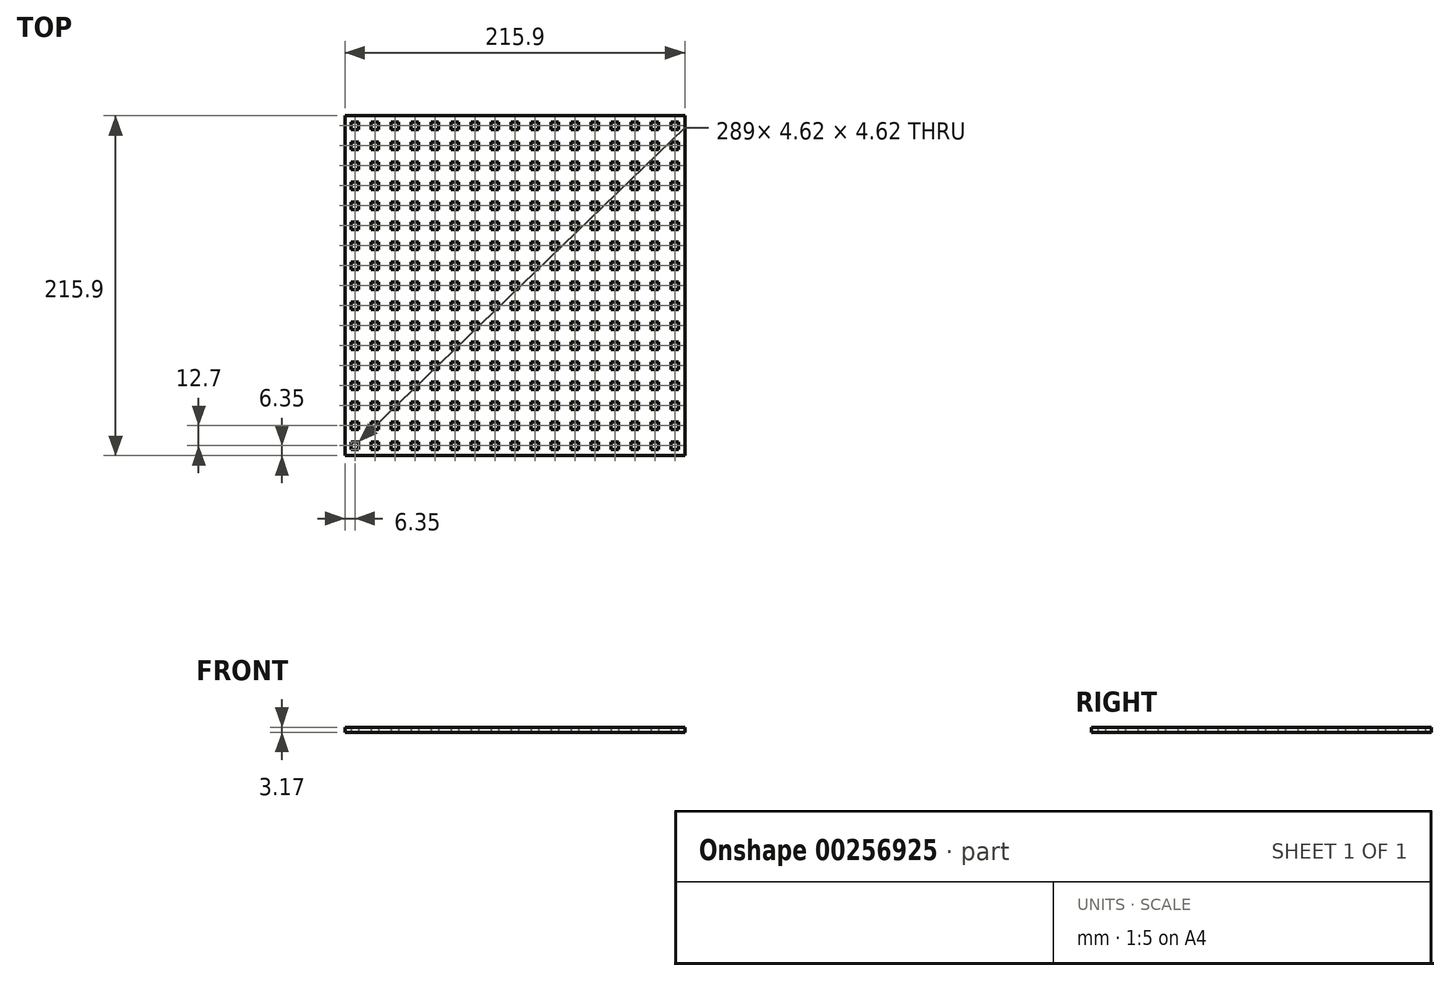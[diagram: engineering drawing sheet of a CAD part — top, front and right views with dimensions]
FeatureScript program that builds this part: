
annotation { "Feature Type Name" : "Feature", "Feature Type Description" : "" }
export const myFeature = defineFeature(function(context is Context, id is Id, definition is map)
    precondition{}
    {
        {
            var Q0;
            Q0=qCreatedBy(makeId("Top.planeOp"),FACE);
            var sketch = newSketch(context, id + "F0", { "sketchPlane" : qUnion([Q0])});
            skLineSegment(sketch, "E0.bottom", {"start": v(107.95, 107.95) * mm, "end": v(-107.95, 107.95) * mm});
            skLineSegment(sketch, "E0.top", {"start": v(107.95, -107.95) * mm, "end": v(-107.95, -107.95) * mm});
            skLineSegment(sketch, "E0.left", {"start": v(107.95, 107.95) * mm, "end": v(107.95, -107.95) * mm});
            skLineSegment(sketch, "E0.right", {"start": v(-107.95, 107.95) * mm, "end": v(-107.95, -107.95) * mm});
            skPoint(sketch, "E0.middle", {"position": v(0, 0) * mm});
            skLineSegment(sketch, "E1.bottom", {"start": v(-107.95, -107.95) * mm, "end": v(-101.6, -107.95) * mm});
            skLineSegment(sketch, "E1.left", {"start": v(-107.95, -107.95) * mm, "end": v(-107.95, -101.6) * mm});
            skLineSegment(sketch, "E2.bottom", {"start": v(-99.29, -103.91) * mm, "end": v(-103.91, -103.91) * mm});
            skLineSegment(sketch, "E2.top", {"start": v(-99.29, -99.29) * mm, "end": v(-103.91, -99.29) * mm});
            skLineSegment(sketch, "E2.left", {"start": v(-99.29, -103.91) * mm, "end": v(-99.29, -99.29) * mm});
            skLineSegment(sketch, "E2.right", {"start": v(-103.91, -103.91) * mm, "end": v(-103.91, -99.29) * mm});
            skPoint(sketch, "E2.middle", {"position": v(-101.6, -101.6) * mm});
            skLineSegment(sketch, "E3.0.1.0", {"start": v(-99.29, -86.59) * mm, "end": v(-103.91, -86.59) * mm});
            skLineSegment(sketch, "E3.0.1.1", {"start": v(-99.29, -91.21) * mm, "end": v(-99.29, -86.59) * mm});
            skLineSegment(sketch, "E3.0.1.2", {"start": v(-99.29, -91.21) * mm, "end": v(-103.91, -91.21) * mm});
            skLineSegment(sketch, "E3.0.1.3", {"start": v(-103.91, -91.21) * mm, "end": v(-103.91, -86.59) * mm});
            skLineSegment(sketch, "E3.0.2.0", {"start": v(-99.29, -73.89) * mm, "end": v(-103.91, -73.89) * mm});
            skLineSegment(sketch, "E3.0.2.1", {"start": v(-99.29, -78.51) * mm, "end": v(-99.29, -73.89) * mm});
            skLineSegment(sketch, "E3.0.2.2", {"start": v(-99.29, -78.51) * mm, "end": v(-103.91, -78.51) * mm});
            skLineSegment(sketch, "E3.0.2.3", {"start": v(-103.91, -78.51) * mm, "end": v(-103.91, -73.89) * mm});
            skLineSegment(sketch, "E3.0.3.0", {"start": v(-99.29, -61.19) * mm, "end": v(-103.91, -61.19) * mm});
            skLineSegment(sketch, "E3.0.3.1", {"start": v(-99.29, -65.81) * mm, "end": v(-99.29, -61.19) * mm});
            skLineSegment(sketch, "E3.0.3.2", {"start": v(-99.29, -65.81) * mm, "end": v(-103.91, -65.81) * mm});
            skLineSegment(sketch, "E3.0.3.3", {"start": v(-103.91, -65.81) * mm, "end": v(-103.91, -61.19) * mm});
            skLineSegment(sketch, "E3.0.4.0", {"start": v(-99.29, -48.49) * mm, "end": v(-103.91, -48.49) * mm});
            skLineSegment(sketch, "E3.0.4.1", {"start": v(-99.29, -53.11) * mm, "end": v(-99.29, -48.49) * mm});
            skLineSegment(sketch, "E3.0.4.2", {"start": v(-99.29, -53.11) * mm, "end": v(-103.91, -53.11) * mm});
            skLineSegment(sketch, "E3.0.4.3", {"start": v(-103.91, -53.11) * mm, "end": v(-103.91, -48.49) * mm});
            skLineSegment(sketch, "E3.0.5.0", {"start": v(-99.29, -35.79) * mm, "end": v(-103.91, -35.79) * mm});
            skLineSegment(sketch, "E3.0.5.1", {"start": v(-99.29, -40.41) * mm, "end": v(-99.29, -35.79) * mm});
            skLineSegment(sketch, "E3.0.5.2", {"start": v(-99.29, -40.41) * mm, "end": v(-103.91, -40.41) * mm});
            skLineSegment(sketch, "E3.0.5.3", {"start": v(-103.91, -40.41) * mm, "end": v(-103.91, -35.79) * mm});
            skLineSegment(sketch, "E3.0.6.0", {"start": v(-99.29, -23.09) * mm, "end": v(-103.91, -23.09) * mm});
            skLineSegment(sketch, "E3.0.6.1", {"start": v(-99.29, -27.71) * mm, "end": v(-99.29, -23.09) * mm});
            skLineSegment(sketch, "E3.0.6.2", {"start": v(-99.29, -27.71) * mm, "end": v(-103.91, -27.71) * mm});
            skLineSegment(sketch, "E3.0.6.3", {"start": v(-103.91, -27.71) * mm, "end": v(-103.91, -23.09) * mm});
            skLineSegment(sketch, "E3.0.7.0", {"start": v(-99.29, -10.39) * mm, "end": v(-103.91, -10.39) * mm});
            skLineSegment(sketch, "E3.0.7.1", {"start": v(-99.29, -15.01) * mm, "end": v(-99.29, -10.39) * mm});
            skLineSegment(sketch, "E3.0.7.2", {"start": v(-99.29, -15.01) * mm, "end": v(-103.91, -15.01) * mm});
            skLineSegment(sketch, "E3.0.7.3", {"start": v(-103.91, -15.01) * mm, "end": v(-103.91, -10.39) * mm});
            skLineSegment(sketch, "E3.0.8.0", {"start": v(-99.29, 2.31) * mm, "end": v(-103.91, 2.31) * mm});
            skLineSegment(sketch, "E3.0.8.1", {"start": v(-99.29, -2.31) * mm, "end": v(-99.29, 2.31) * mm});
            skLineSegment(sketch, "E3.0.8.2", {"start": v(-99.29, -2.31) * mm, "end": v(-103.91, -2.31) * mm});
            skLineSegment(sketch, "E3.0.8.3", {"start": v(-103.91, -2.31) * mm, "end": v(-103.91, 2.31) * mm});
            skLineSegment(sketch, "E3.0.9.0", {"start": v(-99.29, 15.01) * mm, "end": v(-103.91, 15.01) * mm});
            skLineSegment(sketch, "E3.0.9.1", {"start": v(-99.29, 10.39) * mm, "end": v(-99.29, 15.01) * mm});
            skLineSegment(sketch, "E3.0.9.2", {"start": v(-99.29, 10.39) * mm, "end": v(-103.91, 10.39) * mm});
            skLineSegment(sketch, "E3.0.9.3", {"start": v(-103.91, 10.39) * mm, "end": v(-103.91, 15.01) * mm});
            skLineSegment(sketch, "E3.0.10.0", {"start": v(-99.29, 27.71) * mm, "end": v(-103.91, 27.71) * mm});
            skLineSegment(sketch, "E3.0.10.1", {"start": v(-99.29, 23.09) * mm, "end": v(-99.29, 27.71) * mm});
            skLineSegment(sketch, "E3.0.10.2", {"start": v(-99.29, 23.09) * mm, "end": v(-103.91, 23.09) * mm});
            skLineSegment(sketch, "E3.0.10.3", {"start": v(-103.91, 23.09) * mm, "end": v(-103.91, 27.71) * mm});
            skLineSegment(sketch, "E3.0.11.0", {"start": v(-99.29, 40.41) * mm, "end": v(-103.91, 40.41) * mm});
            skLineSegment(sketch, "E3.0.11.1", {"start": v(-99.29, 35.79) * mm, "end": v(-99.29, 40.41) * mm});
            skLineSegment(sketch, "E3.0.11.2", {"start": v(-99.29, 35.79) * mm, "end": v(-103.91, 35.79) * mm});
            skLineSegment(sketch, "E3.0.11.3", {"start": v(-103.91, 35.79) * mm, "end": v(-103.91, 40.41) * mm});
            skLineSegment(sketch, "E3.0.12.0", {"start": v(-99.29, 53.11) * mm, "end": v(-103.91, 53.11) * mm});
            skLineSegment(sketch, "E3.0.12.1", {"start": v(-99.29, 48.49) * mm, "end": v(-99.29, 53.11) * mm});
            skLineSegment(sketch, "E3.0.12.2", {"start": v(-99.29, 48.49) * mm, "end": v(-103.91, 48.49) * mm});
            skLineSegment(sketch, "E3.0.12.3", {"start": v(-103.91, 48.49) * mm, "end": v(-103.91, 53.11) * mm});
            skLineSegment(sketch, "E3.0.13.0", {"start": v(-99.29, 65.81) * mm, "end": v(-103.91, 65.81) * mm});
            skLineSegment(sketch, "E3.0.13.1", {"start": v(-99.29, 61.19) * mm, "end": v(-99.29, 65.81) * mm});
            skLineSegment(sketch, "E3.0.13.2", {"start": v(-99.29, 61.19) * mm, "end": v(-103.91, 61.19) * mm});
            skLineSegment(sketch, "E3.0.13.3", {"start": v(-103.91, 61.19) * mm, "end": v(-103.91, 65.81) * mm});
            skLineSegment(sketch, "E3.0.14.0", {"start": v(-99.29, 78.51) * mm, "end": v(-103.91, 78.51) * mm});
            skLineSegment(sketch, "E3.0.14.1", {"start": v(-99.29, 73.89) * mm, "end": v(-99.29, 78.51) * mm});
            skLineSegment(sketch, "E3.0.14.2", {"start": v(-99.29, 73.89) * mm, "end": v(-103.91, 73.89) * mm});
            skLineSegment(sketch, "E3.0.14.3", {"start": v(-103.91, 73.89) * mm, "end": v(-103.91, 78.51) * mm});
            skLineSegment(sketch, "E3.0.15.0", {"start": v(-99.29, 91.21) * mm, "end": v(-103.91, 91.21) * mm});
            skLineSegment(sketch, "E3.0.15.1", {"start": v(-99.29, 86.59) * mm, "end": v(-99.29, 91.21) * mm});
            skLineSegment(sketch, "E3.0.15.2", {"start": v(-99.29, 86.59) * mm, "end": v(-103.91, 86.59) * mm});
            skLineSegment(sketch, "E3.0.15.3", {"start": v(-103.91, 86.59) * mm, "end": v(-103.91, 91.21) * mm});
            skLineSegment(sketch, "E3.0.16.0", {"start": v(-99.29, 103.91) * mm, "end": v(-103.91, 103.91) * mm});
            skLineSegment(sketch, "E3.0.16.1", {"start": v(-99.29, 99.29) * mm, "end": v(-99.29, 103.91) * mm});
            skLineSegment(sketch, "E3.0.16.2", {"start": v(-99.29, 99.29) * mm, "end": v(-103.91, 99.29) * mm});
            skLineSegment(sketch, "E3.0.16.3", {"start": v(-103.91, 99.29) * mm, "end": v(-103.91, 103.91) * mm});
            skLineSegment(sketch, "E3.1.0.0", {"start": v(-86.59, -99.29) * mm, "end": v(-91.21, -99.29) * mm});
            skLineSegment(sketch, "E3.1.0.1", {"start": v(-86.59, -103.91) * mm, "end": v(-86.59, -99.29) * mm});
            skLineSegment(sketch, "E3.1.0.2", {"start": v(-86.59, -103.91) * mm, "end": v(-91.21, -103.91) * mm});
            skLineSegment(sketch, "E3.1.0.3", {"start": v(-91.21, -103.91) * mm, "end": v(-91.21, -99.29) * mm});
            skLineSegment(sketch, "E3.1.1.0", {"start": v(-86.59, -86.59) * mm, "end": v(-91.21, -86.59) * mm});
            skLineSegment(sketch, "E3.1.1.1", {"start": v(-86.59, -91.21) * mm, "end": v(-86.59, -86.59) * mm});
            skLineSegment(sketch, "E3.1.1.2", {"start": v(-86.59, -91.21) * mm, "end": v(-91.21, -91.21) * mm});
            skLineSegment(sketch, "E3.1.1.3", {"start": v(-91.21, -91.21) * mm, "end": v(-91.21, -86.59) * mm});
            skLineSegment(sketch, "E3.1.2.0", {"start": v(-86.59, -73.89) * mm, "end": v(-91.21, -73.89) * mm});
            skLineSegment(sketch, "E3.1.2.1", {"start": v(-86.59, -78.51) * mm, "end": v(-86.59, -73.89) * mm});
            skLineSegment(sketch, "E3.1.2.2", {"start": v(-86.59, -78.51) * mm, "end": v(-91.21, -78.51) * mm});
            skLineSegment(sketch, "E3.1.2.3", {"start": v(-91.21, -78.51) * mm, "end": v(-91.21, -73.89) * mm});
            skLineSegment(sketch, "E3.1.3.0", {"start": v(-86.59, -61.19) * mm, "end": v(-91.21, -61.19) * mm});
            skLineSegment(sketch, "E3.1.3.1", {"start": v(-86.59, -65.81) * mm, "end": v(-86.59, -61.19) * mm});
            skLineSegment(sketch, "E3.1.3.2", {"start": v(-86.59, -65.81) * mm, "end": v(-91.21, -65.81) * mm});
            skLineSegment(sketch, "E3.1.3.3", {"start": v(-91.21, -65.81) * mm, "end": v(-91.21, -61.19) * mm});
            skLineSegment(sketch, "E3.1.4.0", {"start": v(-86.59, -48.49) * mm, "end": v(-91.21, -48.49) * mm});
            skLineSegment(sketch, "E3.1.4.1", {"start": v(-86.59, -53.11) * mm, "end": v(-86.59, -48.49) * mm});
            skLineSegment(sketch, "E3.1.4.2", {"start": v(-86.59, -53.11) * mm, "end": v(-91.21, -53.11) * mm});
            skLineSegment(sketch, "E3.1.4.3", {"start": v(-91.21, -53.11) * mm, "end": v(-91.21, -48.49) * mm});
            skLineSegment(sketch, "E3.1.5.0", {"start": v(-86.59, -35.79) * mm, "end": v(-91.21, -35.79) * mm});
            skLineSegment(sketch, "E3.1.5.1", {"start": v(-86.59, -40.41) * mm, "end": v(-86.59, -35.79) * mm});
            skLineSegment(sketch, "E3.1.5.2", {"start": v(-86.59, -40.41) * mm, "end": v(-91.21, -40.41) * mm});
            skLineSegment(sketch, "E3.1.5.3", {"start": v(-91.21, -40.41) * mm, "end": v(-91.21, -35.79) * mm});
            skLineSegment(sketch, "E3.1.6.0", {"start": v(-86.59, -23.09) * mm, "end": v(-91.21, -23.09) * mm});
            skLineSegment(sketch, "E3.1.6.1", {"start": v(-86.59, -27.71) * mm, "end": v(-86.59, -23.09) * mm});
            skLineSegment(sketch, "E3.1.6.2", {"start": v(-86.59, -27.71) * mm, "end": v(-91.21, -27.71) * mm});
            skLineSegment(sketch, "E3.1.6.3", {"start": v(-91.21, -27.71) * mm, "end": v(-91.21, -23.09) * mm});
            skLineSegment(sketch, "E3.1.7.0", {"start": v(-86.59, -10.39) * mm, "end": v(-91.21, -10.39) * mm});
            skLineSegment(sketch, "E3.1.7.1", {"start": v(-86.59, -15.01) * mm, "end": v(-86.59, -10.39) * mm});
            skLineSegment(sketch, "E3.1.7.2", {"start": v(-86.59, -15.01) * mm, "end": v(-91.21, -15.01) * mm});
            skLineSegment(sketch, "E3.1.7.3", {"start": v(-91.21, -15.01) * mm, "end": v(-91.21, -10.39) * mm});
            skLineSegment(sketch, "E3.1.8.0", {"start": v(-86.59, 2.31) * mm, "end": v(-91.21, 2.31) * mm});
            skLineSegment(sketch, "E3.1.8.1", {"start": v(-86.59, -2.31) * mm, "end": v(-86.59, 2.31) * mm});
            skLineSegment(sketch, "E3.1.8.2", {"start": v(-86.59, -2.31) * mm, "end": v(-91.21, -2.31) * mm});
            skLineSegment(sketch, "E3.1.8.3", {"start": v(-91.21, -2.31) * mm, "end": v(-91.21, 2.31) * mm});
            skLineSegment(sketch, "E3.1.9.0", {"start": v(-86.59, 15.01) * mm, "end": v(-91.21, 15.01) * mm});
            skLineSegment(sketch, "E3.1.9.1", {"start": v(-86.59, 10.39) * mm, "end": v(-86.59, 15.01) * mm});
            skLineSegment(sketch, "E3.1.9.2", {"start": v(-86.59, 10.39) * mm, "end": v(-91.21, 10.39) * mm});
            skLineSegment(sketch, "E3.1.9.3", {"start": v(-91.21, 10.39) * mm, "end": v(-91.21, 15.01) * mm});
            skLineSegment(sketch, "E3.1.10.0", {"start": v(-86.59, 27.71) * mm, "end": v(-91.21, 27.71) * mm});
            skLineSegment(sketch, "E3.1.10.1", {"start": v(-86.59, 23.09) * mm, "end": v(-86.59, 27.71) * mm});
            skLineSegment(sketch, "E3.1.10.2", {"start": v(-86.59, 23.09) * mm, "end": v(-91.21, 23.09) * mm});
            skLineSegment(sketch, "E3.1.10.3", {"start": v(-91.21, 23.09) * mm, "end": v(-91.21, 27.71) * mm});
            skLineSegment(sketch, "E3.1.11.0", {"start": v(-86.59, 40.41) * mm, "end": v(-91.21, 40.41) * mm});
            skLineSegment(sketch, "E3.1.11.1", {"start": v(-86.59, 35.79) * mm, "end": v(-86.59, 40.41) * mm});
            skLineSegment(sketch, "E3.1.11.2", {"start": v(-86.59, 35.79) * mm, "end": v(-91.21, 35.79) * mm});
            skLineSegment(sketch, "E3.1.11.3", {"start": v(-91.21, 35.79) * mm, "end": v(-91.21, 40.41) * mm});
            skLineSegment(sketch, "E3.1.12.0", {"start": v(-86.59, 53.11) * mm, "end": v(-91.21, 53.11) * mm});
            skLineSegment(sketch, "E3.1.12.1", {"start": v(-86.59, 48.49) * mm, "end": v(-86.59, 53.11) * mm});
            skLineSegment(sketch, "E3.1.12.2", {"start": v(-86.59, 48.49) * mm, "end": v(-91.21, 48.49) * mm});
            skLineSegment(sketch, "E3.1.12.3", {"start": v(-91.21, 48.49) * mm, "end": v(-91.21, 53.11) * mm});
            skLineSegment(sketch, "E3.1.13.0", {"start": v(-86.59, 65.81) * mm, "end": v(-91.21, 65.81) * mm});
            skLineSegment(sketch, "E3.1.13.1", {"start": v(-86.59, 61.19) * mm, "end": v(-86.59, 65.81) * mm});
            skLineSegment(sketch, "E3.1.13.2", {"start": v(-86.59, 61.19) * mm, "end": v(-91.21, 61.19) * mm});
            skLineSegment(sketch, "E3.1.13.3", {"start": v(-91.21, 61.19) * mm, "end": v(-91.21, 65.81) * mm});
            skLineSegment(sketch, "E3.1.14.0", {"start": v(-86.59, 78.51) * mm, "end": v(-91.21, 78.51) * mm});
            skLineSegment(sketch, "E3.1.14.1", {"start": v(-86.59, 73.89) * mm, "end": v(-86.59, 78.51) * mm});
            skLineSegment(sketch, "E3.1.14.2", {"start": v(-86.59, 73.89) * mm, "end": v(-91.21, 73.89) * mm});
            skLineSegment(sketch, "E3.1.14.3", {"start": v(-91.21, 73.89) * mm, "end": v(-91.21, 78.51) * mm});
            skLineSegment(sketch, "E3.1.15.0", {"start": v(-86.59, 91.21) * mm, "end": v(-91.21, 91.21) * mm});
            skLineSegment(sketch, "E3.1.15.1", {"start": v(-86.59, 86.59) * mm, "end": v(-86.59, 91.21) * mm});
            skLineSegment(sketch, "E3.1.15.2", {"start": v(-86.59, 86.59) * mm, "end": v(-91.21, 86.59) * mm});
            skLineSegment(sketch, "E3.1.15.3", {"start": v(-91.21, 86.59) * mm, "end": v(-91.21, 91.21) * mm});
            skLineSegment(sketch, "E3.1.16.0", {"start": v(-86.59, 103.91) * mm, "end": v(-91.21, 103.91) * mm});
            skLineSegment(sketch, "E3.1.16.1", {"start": v(-86.59, 99.29) * mm, "end": v(-86.59, 103.91) * mm});
            skLineSegment(sketch, "E3.1.16.2", {"start": v(-86.59, 99.29) * mm, "end": v(-91.21, 99.29) * mm});
            skLineSegment(sketch, "E3.1.16.3", {"start": v(-91.21, 99.29) * mm, "end": v(-91.21, 103.91) * mm});
            skLineSegment(sketch, "E3.2.0.0", {"start": v(-73.89, -99.29) * mm, "end": v(-78.51, -99.29) * mm});
            skLineSegment(sketch, "E3.2.0.1", {"start": v(-73.89, -103.91) * mm, "end": v(-73.89, -99.29) * mm});
            skLineSegment(sketch, "E3.2.0.2", {"start": v(-73.89, -103.91) * mm, "end": v(-78.51, -103.91) * mm});
            skLineSegment(sketch, "E3.2.0.3", {"start": v(-78.51, -103.91) * mm, "end": v(-78.51, -99.29) * mm});
            skLineSegment(sketch, "E3.2.1.0", {"start": v(-73.89, -86.59) * mm, "end": v(-78.51, -86.59) * mm});
            skLineSegment(sketch, "E3.2.1.1", {"start": v(-73.89, -91.21) * mm, "end": v(-73.89, -86.59) * mm});
            skLineSegment(sketch, "E3.2.1.2", {"start": v(-73.89, -91.21) * mm, "end": v(-78.51, -91.21) * mm});
            skLineSegment(sketch, "E3.2.1.3", {"start": v(-78.51, -91.21) * mm, "end": v(-78.51, -86.59) * mm});
            skLineSegment(sketch, "E3.2.2.0", {"start": v(-73.89, -73.89) * mm, "end": v(-78.51, -73.89) * mm});
            skLineSegment(sketch, "E3.2.2.1", {"start": v(-73.89, -78.51) * mm, "end": v(-73.89, -73.89) * mm});
            skLineSegment(sketch, "E3.2.2.2", {"start": v(-73.89, -78.51) * mm, "end": v(-78.51, -78.51) * mm});
            skLineSegment(sketch, "E3.2.2.3", {"start": v(-78.51, -78.51) * mm, "end": v(-78.51, -73.89) * mm});
            skLineSegment(sketch, "E3.2.3.0", {"start": v(-73.89, -61.19) * mm, "end": v(-78.51, -61.19) * mm});
            skLineSegment(sketch, "E3.2.3.1", {"start": v(-73.89, -65.81) * mm, "end": v(-73.89, -61.19) * mm});
            skLineSegment(sketch, "E3.2.3.2", {"start": v(-73.89, -65.81) * mm, "end": v(-78.51, -65.81) * mm});
            skLineSegment(sketch, "E3.2.3.3", {"start": v(-78.51, -65.81) * mm, "end": v(-78.51, -61.19) * mm});
            skLineSegment(sketch, "E3.2.4.0", {"start": v(-73.89, -48.49) * mm, "end": v(-78.51, -48.49) * mm});
            skLineSegment(sketch, "E3.2.4.1", {"start": v(-73.89, -53.11) * mm, "end": v(-73.89, -48.49) * mm});
            skLineSegment(sketch, "E3.2.4.2", {"start": v(-73.89, -53.11) * mm, "end": v(-78.51, -53.11) * mm});
            skLineSegment(sketch, "E3.2.4.3", {"start": v(-78.51, -53.11) * mm, "end": v(-78.51, -48.49) * mm});
            skLineSegment(sketch, "E3.2.5.0", {"start": v(-73.89, -35.79) * mm, "end": v(-78.51, -35.79) * mm});
            skLineSegment(sketch, "E3.2.5.1", {"start": v(-73.89, -40.41) * mm, "end": v(-73.89, -35.79) * mm});
            skLineSegment(sketch, "E3.2.5.2", {"start": v(-73.89, -40.41) * mm, "end": v(-78.51, -40.41) * mm});
            skLineSegment(sketch, "E3.2.5.3", {"start": v(-78.51, -40.41) * mm, "end": v(-78.51, -35.79) * mm});
            skLineSegment(sketch, "E3.2.6.0", {"start": v(-73.89, -23.09) * mm, "end": v(-78.51, -23.09) * mm});
            skLineSegment(sketch, "E3.2.6.1", {"start": v(-73.89, -27.71) * mm, "end": v(-73.89, -23.09) * mm});
            skLineSegment(sketch, "E3.2.6.2", {"start": v(-73.89, -27.71) * mm, "end": v(-78.51, -27.71) * mm});
            skLineSegment(sketch, "E3.2.6.3", {"start": v(-78.51, -27.71) * mm, "end": v(-78.51, -23.09) * mm});
            skLineSegment(sketch, "E3.2.7.0", {"start": v(-73.89, -10.39) * mm, "end": v(-78.51, -10.39) * mm});
            skLineSegment(sketch, "E3.2.7.1", {"start": v(-73.89, -15.01) * mm, "end": v(-73.89, -10.39) * mm});
            skLineSegment(sketch, "E3.2.7.2", {"start": v(-73.89, -15.01) * mm, "end": v(-78.51, -15.01) * mm});
            skLineSegment(sketch, "E3.2.7.3", {"start": v(-78.51, -15.01) * mm, "end": v(-78.51, -10.39) * mm});
            skLineSegment(sketch, "E3.2.8.0", {"start": v(-73.89, 2.31) * mm, "end": v(-78.51, 2.31) * mm});
            skLineSegment(sketch, "E3.2.8.1", {"start": v(-73.89, -2.31) * mm, "end": v(-73.89, 2.31) * mm});
            skLineSegment(sketch, "E3.2.8.2", {"start": v(-73.89, -2.31) * mm, "end": v(-78.51, -2.31) * mm});
            skLineSegment(sketch, "E3.2.8.3", {"start": v(-78.51, -2.31) * mm, "end": v(-78.51, 2.31) * mm});
            skLineSegment(sketch, "E3.2.9.0", {"start": v(-73.89, 15.01) * mm, "end": v(-78.51, 15.01) * mm});
            skLineSegment(sketch, "E3.2.9.1", {"start": v(-73.89, 10.39) * mm, "end": v(-73.89, 15.01) * mm});
            skLineSegment(sketch, "E3.2.9.2", {"start": v(-73.89, 10.39) * mm, "end": v(-78.51, 10.39) * mm});
            skLineSegment(sketch, "E3.2.9.3", {"start": v(-78.51, 10.39) * mm, "end": v(-78.51, 15.01) * mm});
            skLineSegment(sketch, "E3.2.10.0", {"start": v(-73.89, 27.71) * mm, "end": v(-78.51, 27.71) * mm});
            skLineSegment(sketch, "E3.2.10.1", {"start": v(-73.89, 23.09) * mm, "end": v(-73.89, 27.71) * mm});
            skLineSegment(sketch, "E3.2.10.2", {"start": v(-73.89, 23.09) * mm, "end": v(-78.51, 23.09) * mm});
            skLineSegment(sketch, "E3.2.10.3", {"start": v(-78.51, 23.09) * mm, "end": v(-78.51, 27.71) * mm});
            skLineSegment(sketch, "E3.2.11.0", {"start": v(-73.89, 40.41) * mm, "end": v(-78.51, 40.41) * mm});
            skLineSegment(sketch, "E3.2.11.1", {"start": v(-73.89, 35.79) * mm, "end": v(-73.89, 40.41) * mm});
            skLineSegment(sketch, "E3.2.11.2", {"start": v(-73.89, 35.79) * mm, "end": v(-78.51, 35.79) * mm});
            skLineSegment(sketch, "E3.2.11.3", {"start": v(-78.51, 35.79) * mm, "end": v(-78.51, 40.41) * mm});
            skLineSegment(sketch, "E3.2.12.0", {"start": v(-73.89, 53.11) * mm, "end": v(-78.51, 53.11) * mm});
            skLineSegment(sketch, "E3.2.12.1", {"start": v(-73.89, 48.49) * mm, "end": v(-73.89, 53.11) * mm});
            skLineSegment(sketch, "E3.2.12.2", {"start": v(-73.89, 48.49) * mm, "end": v(-78.51, 48.49) * mm});
            skLineSegment(sketch, "E3.2.12.3", {"start": v(-78.51, 48.49) * mm, "end": v(-78.51, 53.11) * mm});
            skLineSegment(sketch, "E3.2.13.0", {"start": v(-73.89, 65.81) * mm, "end": v(-78.51, 65.81) * mm});
            skLineSegment(sketch, "E3.2.13.1", {"start": v(-73.89, 61.19) * mm, "end": v(-73.89, 65.81) * mm});
            skLineSegment(sketch, "E3.2.13.2", {"start": v(-73.89, 61.19) * mm, "end": v(-78.51, 61.19) * mm});
            skLineSegment(sketch, "E3.2.13.3", {"start": v(-78.51, 61.19) * mm, "end": v(-78.51, 65.81) * mm});
            skLineSegment(sketch, "E3.2.14.0", {"start": v(-73.89, 78.51) * mm, "end": v(-78.51, 78.51) * mm});
            skLineSegment(sketch, "E3.2.14.1", {"start": v(-73.89, 73.89) * mm, "end": v(-73.89, 78.51) * mm});
            skLineSegment(sketch, "E3.2.14.2", {"start": v(-73.89, 73.89) * mm, "end": v(-78.51, 73.89) * mm});
            skLineSegment(sketch, "E3.2.14.3", {"start": v(-78.51, 73.89) * mm, "end": v(-78.51, 78.51) * mm});
            skLineSegment(sketch, "E3.2.15.0", {"start": v(-73.89, 91.21) * mm, "end": v(-78.51, 91.21) * mm});
            skLineSegment(sketch, "E3.2.15.1", {"start": v(-73.89, 86.59) * mm, "end": v(-73.89, 91.21) * mm});
            skLineSegment(sketch, "E3.2.15.2", {"start": v(-73.89, 86.59) * mm, "end": v(-78.51, 86.59) * mm});
            skLineSegment(sketch, "E3.2.15.3", {"start": v(-78.51, 86.59) * mm, "end": v(-78.51, 91.21) * mm});
            skLineSegment(sketch, "E3.2.16.0", {"start": v(-73.89, 103.91) * mm, "end": v(-78.51, 103.91) * mm});
            skLineSegment(sketch, "E3.2.16.1", {"start": v(-73.89, 99.29) * mm, "end": v(-73.89, 103.91) * mm});
            skLineSegment(sketch, "E3.2.16.2", {"start": v(-73.89, 99.29) * mm, "end": v(-78.51, 99.29) * mm});
            skLineSegment(sketch, "E3.2.16.3", {"start": v(-78.51, 99.29) * mm, "end": v(-78.51, 103.91) * mm});
            skLineSegment(sketch, "E3.3.0.0", {"start": v(-61.19, -99.29) * mm, "end": v(-65.81, -99.29) * mm});
            skLineSegment(sketch, "E3.3.0.1", {"start": v(-61.19, -103.91) * mm, "end": v(-61.19, -99.29) * mm});
            skLineSegment(sketch, "E3.3.0.2", {"start": v(-61.19, -103.91) * mm, "end": v(-65.81, -103.91) * mm});
            skLineSegment(sketch, "E3.3.0.3", {"start": v(-65.81, -103.91) * mm, "end": v(-65.81, -99.29) * mm});
            skLineSegment(sketch, "E3.3.1.0", {"start": v(-61.19, -86.59) * mm, "end": v(-65.81, -86.59) * mm});
            skLineSegment(sketch, "E3.3.1.1", {"start": v(-61.19, -91.21) * mm, "end": v(-61.19, -86.59) * mm});
            skLineSegment(sketch, "E3.3.1.2", {"start": v(-61.19, -91.21) * mm, "end": v(-65.81, -91.21) * mm});
            skLineSegment(sketch, "E3.3.1.3", {"start": v(-65.81, -91.21) * mm, "end": v(-65.81, -86.59) * mm});
            skLineSegment(sketch, "E3.3.2.0", {"start": v(-61.19, -73.89) * mm, "end": v(-65.81, -73.89) * mm});
            skLineSegment(sketch, "E3.3.2.1", {"start": v(-61.19, -78.51) * mm, "end": v(-61.19, -73.89) * mm});
            skLineSegment(sketch, "E3.3.2.2", {"start": v(-61.19, -78.51) * mm, "end": v(-65.81, -78.51) * mm});
            skLineSegment(sketch, "E3.3.2.3", {"start": v(-65.81, -78.51) * mm, "end": v(-65.81, -73.89) * mm});
            skLineSegment(sketch, "E3.3.3.0", {"start": v(-61.19, -61.19) * mm, "end": v(-65.81, -61.19) * mm});
            skLineSegment(sketch, "E3.3.3.1", {"start": v(-61.19, -65.81) * mm, "end": v(-61.19, -61.19) * mm});
            skLineSegment(sketch, "E3.3.3.2", {"start": v(-61.19, -65.81) * mm, "end": v(-65.81, -65.81) * mm});
            skLineSegment(sketch, "E3.3.3.3", {"start": v(-65.81, -65.81) * mm, "end": v(-65.81, -61.19) * mm});
            skLineSegment(sketch, "E3.3.4.0", {"start": v(-61.19, -48.49) * mm, "end": v(-65.81, -48.49) * mm});
            skLineSegment(sketch, "E3.3.4.1", {"start": v(-61.19, -53.11) * mm, "end": v(-61.19, -48.49) * mm});
            skLineSegment(sketch, "E3.3.4.2", {"start": v(-61.19, -53.11) * mm, "end": v(-65.81, -53.11) * mm});
            skLineSegment(sketch, "E3.3.4.3", {"start": v(-65.81, -53.11) * mm, "end": v(-65.81, -48.49) * mm});
            skLineSegment(sketch, "E3.3.5.0", {"start": v(-61.19, -35.79) * mm, "end": v(-65.81, -35.79) * mm});
            skLineSegment(sketch, "E3.3.5.1", {"start": v(-61.19, -40.41) * mm, "end": v(-61.19, -35.79) * mm});
            skLineSegment(sketch, "E3.3.5.2", {"start": v(-61.19, -40.41) * mm, "end": v(-65.81, -40.41) * mm});
            skLineSegment(sketch, "E3.3.5.3", {"start": v(-65.81, -40.41) * mm, "end": v(-65.81, -35.79) * mm});
            skLineSegment(sketch, "E3.3.6.0", {"start": v(-61.19, -23.09) * mm, "end": v(-65.81, -23.09) * mm});
            skLineSegment(sketch, "E3.3.6.1", {"start": v(-61.19, -27.71) * mm, "end": v(-61.19, -23.09) * mm});
            skLineSegment(sketch, "E3.3.6.2", {"start": v(-61.19, -27.71) * mm, "end": v(-65.81, -27.71) * mm});
            skLineSegment(sketch, "E3.3.6.3", {"start": v(-65.81, -27.71) * mm, "end": v(-65.81, -23.09) * mm});
            skLineSegment(sketch, "E3.3.7.0", {"start": v(-61.19, -10.39) * mm, "end": v(-65.81, -10.39) * mm});
            skLineSegment(sketch, "E3.3.7.1", {"start": v(-61.19, -15.01) * mm, "end": v(-61.19, -10.39) * mm});
            skLineSegment(sketch, "E3.3.7.2", {"start": v(-61.19, -15.01) * mm, "end": v(-65.81, -15.01) * mm});
            skLineSegment(sketch, "E3.3.7.3", {"start": v(-65.81, -15.01) * mm, "end": v(-65.81, -10.39) * mm});
            skLineSegment(sketch, "E3.3.8.0", {"start": v(-61.19, 2.31) * mm, "end": v(-65.81, 2.31) * mm});
            skLineSegment(sketch, "E3.3.8.1", {"start": v(-61.19, -2.31) * mm, "end": v(-61.19, 2.31) * mm});
            skLineSegment(sketch, "E3.3.8.2", {"start": v(-61.19, -2.31) * mm, "end": v(-65.81, -2.31) * mm});
            skLineSegment(sketch, "E3.3.8.3", {"start": v(-65.81, -2.31) * mm, "end": v(-65.81, 2.31) * mm});
            skLineSegment(sketch, "E3.3.9.0", {"start": v(-61.19, 15.01) * mm, "end": v(-65.81, 15.01) * mm});
            skLineSegment(sketch, "E3.3.9.1", {"start": v(-61.19, 10.39) * mm, "end": v(-61.19, 15.01) * mm});
            skLineSegment(sketch, "E3.3.9.2", {"start": v(-61.19, 10.39) * mm, "end": v(-65.81, 10.39) * mm});
            skLineSegment(sketch, "E3.3.9.3", {"start": v(-65.81, 10.39) * mm, "end": v(-65.81, 15.01) * mm});
            skLineSegment(sketch, "E3.3.10.0", {"start": v(-61.19, 27.71) * mm, "end": v(-65.81, 27.71) * mm});
            skLineSegment(sketch, "E3.3.10.1", {"start": v(-61.19, 23.09) * mm, "end": v(-61.19, 27.71) * mm});
            skLineSegment(sketch, "E3.3.10.2", {"start": v(-61.19, 23.09) * mm, "end": v(-65.81, 23.09) * mm});
            skLineSegment(sketch, "E3.3.10.3", {"start": v(-65.81, 23.09) * mm, "end": v(-65.81, 27.71) * mm});
            skLineSegment(sketch, "E3.3.11.0", {"start": v(-61.19, 40.41) * mm, "end": v(-65.81, 40.41) * mm});
            skLineSegment(sketch, "E3.3.11.1", {"start": v(-61.19, 35.79) * mm, "end": v(-61.19, 40.41) * mm});
            skLineSegment(sketch, "E3.3.11.2", {"start": v(-61.19, 35.79) * mm, "end": v(-65.81, 35.79) * mm});
            skLineSegment(sketch, "E3.3.11.3", {"start": v(-65.81, 35.79) * mm, "end": v(-65.81, 40.41) * mm});
            skLineSegment(sketch, "E3.3.12.0", {"start": v(-61.19, 53.11) * mm, "end": v(-65.81, 53.11) * mm});
            skLineSegment(sketch, "E3.3.12.1", {"start": v(-61.19, 48.49) * mm, "end": v(-61.19, 53.11) * mm});
            skLineSegment(sketch, "E3.3.12.2", {"start": v(-61.19, 48.49) * mm, "end": v(-65.81, 48.49) * mm});
            skLineSegment(sketch, "E3.3.12.3", {"start": v(-65.81, 48.49) * mm, "end": v(-65.81, 53.11) * mm});
            skLineSegment(sketch, "E3.3.13.0", {"start": v(-61.19, 65.81) * mm, "end": v(-65.81, 65.81) * mm});
            skLineSegment(sketch, "E3.3.13.1", {"start": v(-61.19, 61.19) * mm, "end": v(-61.19, 65.81) * mm});
            skLineSegment(sketch, "E3.3.13.2", {"start": v(-61.19, 61.19) * mm, "end": v(-65.81, 61.19) * mm});
            skLineSegment(sketch, "E3.3.13.3", {"start": v(-65.81, 61.19) * mm, "end": v(-65.81, 65.81) * mm});
            skLineSegment(sketch, "E3.3.14.0", {"start": v(-61.19, 78.51) * mm, "end": v(-65.81, 78.51) * mm});
            skLineSegment(sketch, "E3.3.14.1", {"start": v(-61.19, 73.89) * mm, "end": v(-61.19, 78.51) * mm});
            skLineSegment(sketch, "E3.3.14.2", {"start": v(-61.19, 73.89) * mm, "end": v(-65.81, 73.89) * mm});
            skLineSegment(sketch, "E3.3.14.3", {"start": v(-65.81, 73.89) * mm, "end": v(-65.81, 78.51) * mm});
            skLineSegment(sketch, "E3.3.15.0", {"start": v(-61.19, 91.21) * mm, "end": v(-65.81, 91.21) * mm});
            skLineSegment(sketch, "E3.3.15.1", {"start": v(-61.19, 86.59) * mm, "end": v(-61.19, 91.21) * mm});
            skLineSegment(sketch, "E3.3.15.2", {"start": v(-61.19, 86.59) * mm, "end": v(-65.81, 86.59) * mm});
            skLineSegment(sketch, "E3.3.15.3", {"start": v(-65.81, 86.59) * mm, "end": v(-65.81, 91.21) * mm});
            skLineSegment(sketch, "E3.3.16.0", {"start": v(-61.19, 103.91) * mm, "end": v(-65.81, 103.91) * mm});
            skLineSegment(sketch, "E3.3.16.1", {"start": v(-61.19, 99.29) * mm, "end": v(-61.19, 103.91) * mm});
            skLineSegment(sketch, "E3.3.16.2", {"start": v(-61.19, 99.29) * mm, "end": v(-65.81, 99.29) * mm});
            skLineSegment(sketch, "E3.3.16.3", {"start": v(-65.81, 99.29) * mm, "end": v(-65.81, 103.91) * mm});
            skLineSegment(sketch, "E3.4.0.0", {"start": v(-48.49, -99.29) * mm, "end": v(-53.11, -99.29) * mm});
            skLineSegment(sketch, "E3.4.0.1", {"start": v(-48.49, -103.91) * mm, "end": v(-48.49, -99.29) * mm});
            skLineSegment(sketch, "E3.4.0.2", {"start": v(-48.49, -103.91) * mm, "end": v(-53.11, -103.91) * mm});
            skLineSegment(sketch, "E3.4.0.3", {"start": v(-53.11, -103.91) * mm, "end": v(-53.11, -99.29) * mm});
            skLineSegment(sketch, "E3.4.1.0", {"start": v(-48.49, -86.59) * mm, "end": v(-53.11, -86.59) * mm});
            skLineSegment(sketch, "E3.4.1.1", {"start": v(-48.49, -91.21) * mm, "end": v(-48.49, -86.59) * mm});
            skLineSegment(sketch, "E3.4.1.2", {"start": v(-48.49, -91.21) * mm, "end": v(-53.11, -91.21) * mm});
            skLineSegment(sketch, "E3.4.1.3", {"start": v(-53.11, -91.21) * mm, "end": v(-53.11, -86.59) * mm});
            skLineSegment(sketch, "E3.4.2.0", {"start": v(-48.49, -73.89) * mm, "end": v(-53.11, -73.89) * mm});
            skLineSegment(sketch, "E3.4.2.1", {"start": v(-48.49, -78.51) * mm, "end": v(-48.49, -73.89) * mm});
            skLineSegment(sketch, "E3.4.2.2", {"start": v(-48.49, -78.51) * mm, "end": v(-53.11, -78.51) * mm});
            skLineSegment(sketch, "E3.4.2.3", {"start": v(-53.11, -78.51) * mm, "end": v(-53.11, -73.89) * mm});
            skLineSegment(sketch, "E3.4.3.0", {"start": v(-48.49, -61.19) * mm, "end": v(-53.11, -61.19) * mm});
            skLineSegment(sketch, "E3.4.3.1", {"start": v(-48.49, -65.81) * mm, "end": v(-48.49, -61.19) * mm});
            skLineSegment(sketch, "E3.4.3.2", {"start": v(-48.49, -65.81) * mm, "end": v(-53.11, -65.81) * mm});
            skLineSegment(sketch, "E3.4.3.3", {"start": v(-53.11, -65.81) * mm, "end": v(-53.11, -61.19) * mm});
            skLineSegment(sketch, "E3.4.4.0", {"start": v(-48.49, -48.49) * mm, "end": v(-53.11, -48.49) * mm});
            skLineSegment(sketch, "E3.4.4.1", {"start": v(-48.49, -53.11) * mm, "end": v(-48.49, -48.49) * mm});
            skLineSegment(sketch, "E3.4.4.2", {"start": v(-48.49, -53.11) * mm, "end": v(-53.11, -53.11) * mm});
            skLineSegment(sketch, "E3.4.4.3", {"start": v(-53.11, -53.11) * mm, "end": v(-53.11, -48.49) * mm});
            skLineSegment(sketch, "E3.4.5.0", {"start": v(-48.49, -35.79) * mm, "end": v(-53.11, -35.79) * mm});
            skLineSegment(sketch, "E3.4.5.1", {"start": v(-48.49, -40.41) * mm, "end": v(-48.49, -35.79) * mm});
            skLineSegment(sketch, "E3.4.5.2", {"start": v(-48.49, -40.41) * mm, "end": v(-53.11, -40.41) * mm});
            skLineSegment(sketch, "E3.4.5.3", {"start": v(-53.11, -40.41) * mm, "end": v(-53.11, -35.79) * mm});
            skLineSegment(sketch, "E3.4.6.0", {"start": v(-48.49, -23.09) * mm, "end": v(-53.11, -23.09) * mm});
            skLineSegment(sketch, "E3.4.6.1", {"start": v(-48.49, -27.71) * mm, "end": v(-48.49, -23.09) * mm});
            skLineSegment(sketch, "E3.4.6.2", {"start": v(-48.49, -27.71) * mm, "end": v(-53.11, -27.71) * mm});
            skLineSegment(sketch, "E3.4.6.3", {"start": v(-53.11, -27.71) * mm, "end": v(-53.11, -23.09) * mm});
            skLineSegment(sketch, "E3.4.7.0", {"start": v(-48.49, -10.39) * mm, "end": v(-53.11, -10.39) * mm});
            skLineSegment(sketch, "E3.4.7.1", {"start": v(-48.49, -15.01) * mm, "end": v(-48.49, -10.39) * mm});
            skLineSegment(sketch, "E3.4.7.2", {"start": v(-48.49, -15.01) * mm, "end": v(-53.11, -15.01) * mm});
            skLineSegment(sketch, "E3.4.7.3", {"start": v(-53.11, -15.01) * mm, "end": v(-53.11, -10.39) * mm});
            skLineSegment(sketch, "E3.4.8.0", {"start": v(-48.49, 2.31) * mm, "end": v(-53.11, 2.31) * mm});
            skLineSegment(sketch, "E3.4.8.1", {"start": v(-48.49, -2.31) * mm, "end": v(-48.49, 2.31) * mm});
            skLineSegment(sketch, "E3.4.8.2", {"start": v(-48.49, -2.31) * mm, "end": v(-53.11, -2.31) * mm});
            skLineSegment(sketch, "E3.4.8.3", {"start": v(-53.11, -2.31) * mm, "end": v(-53.11, 2.31) * mm});
            skLineSegment(sketch, "E3.4.9.0", {"start": v(-48.49, 15.01) * mm, "end": v(-53.11, 15.01) * mm});
            skLineSegment(sketch, "E3.4.9.1", {"start": v(-48.49, 10.39) * mm, "end": v(-48.49, 15.01) * mm});
            skLineSegment(sketch, "E3.4.9.2", {"start": v(-48.49, 10.39) * mm, "end": v(-53.11, 10.39) * mm});
            skLineSegment(sketch, "E3.4.9.3", {"start": v(-53.11, 10.39) * mm, "end": v(-53.11, 15.01) * mm});
            skLineSegment(sketch, "E3.4.10.0", {"start": v(-48.49, 27.71) * mm, "end": v(-53.11, 27.71) * mm});
            skLineSegment(sketch, "E3.4.10.1", {"start": v(-48.49, 23.09) * mm, "end": v(-48.49, 27.71) * mm});
            skLineSegment(sketch, "E3.4.10.2", {"start": v(-48.49, 23.09) * mm, "end": v(-53.11, 23.09) * mm});
            skLineSegment(sketch, "E3.4.10.3", {"start": v(-53.11, 23.09) * mm, "end": v(-53.11, 27.71) * mm});
            skLineSegment(sketch, "E3.4.11.0", {"start": v(-48.49, 40.41) * mm, "end": v(-53.11, 40.41) * mm});
            skLineSegment(sketch, "E3.4.11.1", {"start": v(-48.49, 35.79) * mm, "end": v(-48.49, 40.41) * mm});
            skLineSegment(sketch, "E3.4.11.2", {"start": v(-48.49, 35.79) * mm, "end": v(-53.11, 35.79) * mm});
            skLineSegment(sketch, "E3.4.11.3", {"start": v(-53.11, 35.79) * mm, "end": v(-53.11, 40.41) * mm});
            skLineSegment(sketch, "E3.4.12.0", {"start": v(-48.49, 53.11) * mm, "end": v(-53.11, 53.11) * mm});
            skLineSegment(sketch, "E3.4.12.1", {"start": v(-48.49, 48.49) * mm, "end": v(-48.49, 53.11) * mm});
            skLineSegment(sketch, "E3.4.12.2", {"start": v(-48.49, 48.49) * mm, "end": v(-53.11, 48.49) * mm});
            skLineSegment(sketch, "E3.4.12.3", {"start": v(-53.11, 48.49) * mm, "end": v(-53.11, 53.11) * mm});
            skLineSegment(sketch, "E3.4.13.0", {"start": v(-48.49, 65.81) * mm, "end": v(-53.11, 65.81) * mm});
            skLineSegment(sketch, "E3.4.13.1", {"start": v(-48.49, 61.19) * mm, "end": v(-48.49, 65.81) * mm});
            skLineSegment(sketch, "E3.4.13.2", {"start": v(-48.49, 61.19) * mm, "end": v(-53.11, 61.19) * mm});
            skLineSegment(sketch, "E3.4.13.3", {"start": v(-53.11, 61.19) * mm, "end": v(-53.11, 65.81) * mm});
            skLineSegment(sketch, "E3.4.14.0", {"start": v(-48.49, 78.51) * mm, "end": v(-53.11, 78.51) * mm});
            skLineSegment(sketch, "E3.4.14.1", {"start": v(-48.49, 73.89) * mm, "end": v(-48.49, 78.51) * mm});
            skLineSegment(sketch, "E3.4.14.2", {"start": v(-48.49, 73.89) * mm, "end": v(-53.11, 73.89) * mm});
            skLineSegment(sketch, "E3.4.14.3", {"start": v(-53.11, 73.89) * mm, "end": v(-53.11, 78.51) * mm});
            skLineSegment(sketch, "E3.4.15.0", {"start": v(-48.49, 91.21) * mm, "end": v(-53.11, 91.21) * mm});
            skLineSegment(sketch, "E3.4.15.1", {"start": v(-48.49, 86.59) * mm, "end": v(-48.49, 91.21) * mm});
            skLineSegment(sketch, "E3.4.15.2", {"start": v(-48.49, 86.59) * mm, "end": v(-53.11, 86.59) * mm});
            skLineSegment(sketch, "E3.4.15.3", {"start": v(-53.11, 86.59) * mm, "end": v(-53.11, 91.21) * mm});
            skLineSegment(sketch, "E3.4.16.0", {"start": v(-48.49, 103.91) * mm, "end": v(-53.11, 103.91) * mm});
            skLineSegment(sketch, "E3.4.16.1", {"start": v(-48.49, 99.29) * mm, "end": v(-48.49, 103.91) * mm});
            skLineSegment(sketch, "E3.4.16.2", {"start": v(-48.49, 99.29) * mm, "end": v(-53.11, 99.29) * mm});
            skLineSegment(sketch, "E3.4.16.3", {"start": v(-53.11, 99.29) * mm, "end": v(-53.11, 103.91) * mm});
            skLineSegment(sketch, "E3.5.0.0", {"start": v(-35.79, -99.29) * mm, "end": v(-40.41, -99.29) * mm});
            skLineSegment(sketch, "E3.5.0.1", {"start": v(-35.79, -103.91) * mm, "end": v(-35.79, -99.29) * mm});
            skLineSegment(sketch, "E3.5.0.2", {"start": v(-35.79, -103.91) * mm, "end": v(-40.41, -103.91) * mm});
            skLineSegment(sketch, "E3.5.0.3", {"start": v(-40.41, -103.91) * mm, "end": v(-40.41, -99.29) * mm});
            skLineSegment(sketch, "E3.5.1.0", {"start": v(-35.79, -86.59) * mm, "end": v(-40.41, -86.59) * mm});
            skLineSegment(sketch, "E3.5.1.1", {"start": v(-35.79, -91.21) * mm, "end": v(-35.79, -86.59) * mm});
            skLineSegment(sketch, "E3.5.1.2", {"start": v(-35.79, -91.21) * mm, "end": v(-40.41, -91.21) * mm});
            skLineSegment(sketch, "E3.5.1.3", {"start": v(-40.41, -91.21) * mm, "end": v(-40.41, -86.59) * mm});
            skLineSegment(sketch, "E3.5.2.0", {"start": v(-35.79, -73.89) * mm, "end": v(-40.41, -73.89) * mm});
            skLineSegment(sketch, "E3.5.2.1", {"start": v(-35.79, -78.51) * mm, "end": v(-35.79, -73.89) * mm});
            skLineSegment(sketch, "E3.5.2.2", {"start": v(-35.79, -78.51) * mm, "end": v(-40.41, -78.51) * mm});
            skLineSegment(sketch, "E3.5.2.3", {"start": v(-40.41, -78.51) * mm, "end": v(-40.41, -73.89) * mm});
            skLineSegment(sketch, "E3.5.3.0", {"start": v(-35.79, -61.19) * mm, "end": v(-40.41, -61.19) * mm});
            skLineSegment(sketch, "E3.5.3.1", {"start": v(-35.79, -65.81) * mm, "end": v(-35.79, -61.19) * mm});
            skLineSegment(sketch, "E3.5.3.2", {"start": v(-35.79, -65.81) * mm, "end": v(-40.41, -65.81) * mm});
            skLineSegment(sketch, "E3.5.3.3", {"start": v(-40.41, -65.81) * mm, "end": v(-40.41, -61.19) * mm});
            skLineSegment(sketch, "E3.5.4.0", {"start": v(-35.79, -48.49) * mm, "end": v(-40.41, -48.49) * mm});
            skLineSegment(sketch, "E3.5.4.1", {"start": v(-35.79, -53.11) * mm, "end": v(-35.79, -48.49) * mm});
            skLineSegment(sketch, "E3.5.4.2", {"start": v(-35.79, -53.11) * mm, "end": v(-40.41, -53.11) * mm});
            skLineSegment(sketch, "E3.5.4.3", {"start": v(-40.41, -53.11) * mm, "end": v(-40.41, -48.49) * mm});
            skLineSegment(sketch, "E3.5.5.0", {"start": v(-35.79, -35.79) * mm, "end": v(-40.41, -35.79) * mm});
            skLineSegment(sketch, "E3.5.5.1", {"start": v(-35.79, -40.41) * mm, "end": v(-35.79, -35.79) * mm});
            skLineSegment(sketch, "E3.5.5.2", {"start": v(-35.79, -40.41) * mm, "end": v(-40.41, -40.41) * mm});
            skLineSegment(sketch, "E3.5.5.3", {"start": v(-40.41, -40.41) * mm, "end": v(-40.41, -35.79) * mm});
            skLineSegment(sketch, "E3.5.6.0", {"start": v(-35.79, -23.09) * mm, "end": v(-40.41, -23.09) * mm});
            skLineSegment(sketch, "E3.5.6.1", {"start": v(-35.79, -27.71) * mm, "end": v(-35.79, -23.09) * mm});
            skLineSegment(sketch, "E3.5.6.2", {"start": v(-35.79, -27.71) * mm, "end": v(-40.41, -27.71) * mm});
            skLineSegment(sketch, "E3.5.6.3", {"start": v(-40.41, -27.71) * mm, "end": v(-40.41, -23.09) * mm});
            skLineSegment(sketch, "E3.5.7.0", {"start": v(-35.79, -10.39) * mm, "end": v(-40.41, -10.39) * mm});
            skLineSegment(sketch, "E3.5.7.1", {"start": v(-35.79, -15.01) * mm, "end": v(-35.79, -10.39) * mm});
            skLineSegment(sketch, "E3.5.7.2", {"start": v(-35.79, -15.01) * mm, "end": v(-40.41, -15.01) * mm});
            skLineSegment(sketch, "E3.5.7.3", {"start": v(-40.41, -15.01) * mm, "end": v(-40.41, -10.39) * mm});
            skLineSegment(sketch, "E3.5.8.0", {"start": v(-35.79, 2.31) * mm, "end": v(-40.41, 2.31) * mm});
            skLineSegment(sketch, "E3.5.8.1", {"start": v(-35.79, -2.31) * mm, "end": v(-35.79, 2.31) * mm});
            skLineSegment(sketch, "E3.5.8.2", {"start": v(-35.79, -2.31) * mm, "end": v(-40.41, -2.31) * mm});
            skLineSegment(sketch, "E3.5.8.3", {"start": v(-40.41, -2.31) * mm, "end": v(-40.41, 2.31) * mm});
            skLineSegment(sketch, "E3.5.9.0", {"start": v(-35.79, 15.01) * mm, "end": v(-40.41, 15.01) * mm});
            skLineSegment(sketch, "E3.5.9.1", {"start": v(-35.79, 10.39) * mm, "end": v(-35.79, 15.01) * mm});
            skLineSegment(sketch, "E3.5.9.2", {"start": v(-35.79, 10.39) * mm, "end": v(-40.41, 10.39) * mm});
            skLineSegment(sketch, "E3.5.9.3", {"start": v(-40.41, 10.39) * mm, "end": v(-40.41, 15.01) * mm});
            skLineSegment(sketch, "E3.5.10.0", {"start": v(-35.79, 27.71) * mm, "end": v(-40.41, 27.71) * mm});
            skLineSegment(sketch, "E3.5.10.1", {"start": v(-35.79, 23.09) * mm, "end": v(-35.79, 27.71) * mm});
            skLineSegment(sketch, "E3.5.10.2", {"start": v(-35.79, 23.09) * mm, "end": v(-40.41, 23.09) * mm});
            skLineSegment(sketch, "E3.5.10.3", {"start": v(-40.41, 23.09) * mm, "end": v(-40.41, 27.71) * mm});
            skLineSegment(sketch, "E3.5.11.0", {"start": v(-35.79, 40.41) * mm, "end": v(-40.41, 40.41) * mm});
            skLineSegment(sketch, "E3.5.11.1", {"start": v(-35.79, 35.79) * mm, "end": v(-35.79, 40.41) * mm});
            skLineSegment(sketch, "E3.5.11.2", {"start": v(-35.79, 35.79) * mm, "end": v(-40.41, 35.79) * mm});
            skLineSegment(sketch, "E3.5.11.3", {"start": v(-40.41, 35.79) * mm, "end": v(-40.41, 40.41) * mm});
            skLineSegment(sketch, "E3.5.12.0", {"start": v(-35.79, 53.11) * mm, "end": v(-40.41, 53.11) * mm});
            skLineSegment(sketch, "E3.5.12.1", {"start": v(-35.79, 48.49) * mm, "end": v(-35.79, 53.11) * mm});
            skLineSegment(sketch, "E3.5.12.2", {"start": v(-35.79, 48.49) * mm, "end": v(-40.41, 48.49) * mm});
            skLineSegment(sketch, "E3.5.12.3", {"start": v(-40.41, 48.49) * mm, "end": v(-40.41, 53.11) * mm});
            skLineSegment(sketch, "E3.5.13.0", {"start": v(-35.79, 65.81) * mm, "end": v(-40.41, 65.81) * mm});
            skLineSegment(sketch, "E3.5.13.1", {"start": v(-35.79, 61.19) * mm, "end": v(-35.79, 65.81) * mm});
            skLineSegment(sketch, "E3.5.13.2", {"start": v(-35.79, 61.19) * mm, "end": v(-40.41, 61.19) * mm});
            skLineSegment(sketch, "E3.5.13.3", {"start": v(-40.41, 61.19) * mm, "end": v(-40.41, 65.81) * mm});
            skLineSegment(sketch, "E3.5.14.0", {"start": v(-35.79, 78.51) * mm, "end": v(-40.41, 78.51) * mm});
            skLineSegment(sketch, "E3.5.14.1", {"start": v(-35.79, 73.89) * mm, "end": v(-35.79, 78.51) * mm});
            skLineSegment(sketch, "E3.5.14.2", {"start": v(-35.79, 73.89) * mm, "end": v(-40.41, 73.89) * mm});
            skLineSegment(sketch, "E3.5.14.3", {"start": v(-40.41, 73.89) * mm, "end": v(-40.41, 78.51) * mm});
            skLineSegment(sketch, "E3.5.15.0", {"start": v(-35.79, 91.21) * mm, "end": v(-40.41, 91.21) * mm});
            skLineSegment(sketch, "E3.5.15.1", {"start": v(-35.79, 86.59) * mm, "end": v(-35.79, 91.21) * mm});
            skLineSegment(sketch, "E3.5.15.2", {"start": v(-35.79, 86.59) * mm, "end": v(-40.41, 86.59) * mm});
            skLineSegment(sketch, "E3.5.15.3", {"start": v(-40.41, 86.59) * mm, "end": v(-40.41, 91.21) * mm});
            skLineSegment(sketch, "E3.5.16.0", {"start": v(-35.79, 103.91) * mm, "end": v(-40.41, 103.91) * mm});
            skLineSegment(sketch, "E3.5.16.1", {"start": v(-35.79, 99.29) * mm, "end": v(-35.79, 103.91) * mm});
            skLineSegment(sketch, "E3.5.16.2", {"start": v(-35.79, 99.29) * mm, "end": v(-40.41, 99.29) * mm});
            skLineSegment(sketch, "E3.5.16.3", {"start": v(-40.41, 99.29) * mm, "end": v(-40.41, 103.91) * mm});
            skLineSegment(sketch, "E3.6.0.0", {"start": v(-23.09, -99.29) * mm, "end": v(-27.71, -99.29) * mm});
            skLineSegment(sketch, "E3.6.0.1", {"start": v(-23.09, -103.91) * mm, "end": v(-23.09, -99.29) * mm});
            skLineSegment(sketch, "E3.6.0.2", {"start": v(-23.09, -103.91) * mm, "end": v(-27.71, -103.91) * mm});
            skLineSegment(sketch, "E3.6.0.3", {"start": v(-27.71, -103.91) * mm, "end": v(-27.71, -99.29) * mm});
            skLineSegment(sketch, "E3.6.1.0", {"start": v(-23.09, -86.59) * mm, "end": v(-27.71, -86.59) * mm});
            skLineSegment(sketch, "E3.6.1.1", {"start": v(-23.09, -91.21) * mm, "end": v(-23.09, -86.59) * mm});
            skLineSegment(sketch, "E3.6.1.2", {"start": v(-23.09, -91.21) * mm, "end": v(-27.71, -91.21) * mm});
            skLineSegment(sketch, "E3.6.1.3", {"start": v(-27.71, -91.21) * mm, "end": v(-27.71, -86.59) * mm});
            skLineSegment(sketch, "E3.6.2.0", {"start": v(-23.09, -73.89) * mm, "end": v(-27.71, -73.89) * mm});
            skLineSegment(sketch, "E3.6.2.1", {"start": v(-23.09, -78.51) * mm, "end": v(-23.09, -73.89) * mm});
            skLineSegment(sketch, "E3.6.2.2", {"start": v(-23.09, -78.51) * mm, "end": v(-27.71, -78.51) * mm});
            skLineSegment(sketch, "E3.6.2.3", {"start": v(-27.71, -78.51) * mm, "end": v(-27.71, -73.89) * mm});
            skLineSegment(sketch, "E3.6.3.0", {"start": v(-23.09, -61.19) * mm, "end": v(-27.71, -61.19) * mm});
            skLineSegment(sketch, "E3.6.3.1", {"start": v(-23.09, -65.81) * mm, "end": v(-23.09, -61.19) * mm});
            skLineSegment(sketch, "E3.6.3.2", {"start": v(-23.09, -65.81) * mm, "end": v(-27.71, -65.81) * mm});
            skLineSegment(sketch, "E3.6.3.3", {"start": v(-27.71, -65.81) * mm, "end": v(-27.71, -61.19) * mm});
            skLineSegment(sketch, "E3.6.4.0", {"start": v(-23.09, -48.49) * mm, "end": v(-27.71, -48.49) * mm});
            skLineSegment(sketch, "E3.6.4.1", {"start": v(-23.09, -53.11) * mm, "end": v(-23.09, -48.49) * mm});
            skLineSegment(sketch, "E3.6.4.2", {"start": v(-23.09, -53.11) * mm, "end": v(-27.71, -53.11) * mm});
            skLineSegment(sketch, "E3.6.4.3", {"start": v(-27.71, -53.11) * mm, "end": v(-27.71, -48.49) * mm});
            skLineSegment(sketch, "E3.6.5.0", {"start": v(-23.09, -35.79) * mm, "end": v(-27.71, -35.79) * mm});
            skLineSegment(sketch, "E3.6.5.1", {"start": v(-23.09, -40.41) * mm, "end": v(-23.09, -35.79) * mm});
            skLineSegment(sketch, "E3.6.5.2", {"start": v(-23.09, -40.41) * mm, "end": v(-27.71, -40.41) * mm});
            skLineSegment(sketch, "E3.6.5.3", {"start": v(-27.71, -40.41) * mm, "end": v(-27.71, -35.79) * mm});
            skLineSegment(sketch, "E3.6.6.0", {"start": v(-23.09, -23.09) * mm, "end": v(-27.71, -23.09) * mm});
            skLineSegment(sketch, "E3.6.6.1", {"start": v(-23.09, -27.71) * mm, "end": v(-23.09, -23.09) * mm});
            skLineSegment(sketch, "E3.6.6.2", {"start": v(-23.09, -27.71) * mm, "end": v(-27.71, -27.71) * mm});
            skLineSegment(sketch, "E3.6.6.3", {"start": v(-27.71, -27.71) * mm, "end": v(-27.71, -23.09) * mm});
            skLineSegment(sketch, "E3.6.7.0", {"start": v(-23.09, -10.39) * mm, "end": v(-27.71, -10.39) * mm});
            skLineSegment(sketch, "E3.6.7.1", {"start": v(-23.09, -15.01) * mm, "end": v(-23.09, -10.39) * mm});
            skLineSegment(sketch, "E3.6.7.2", {"start": v(-23.09, -15.01) * mm, "end": v(-27.71, -15.01) * mm});
            skLineSegment(sketch, "E3.6.7.3", {"start": v(-27.71, -15.01) * mm, "end": v(-27.71, -10.39) * mm});
            skLineSegment(sketch, "E3.6.8.0", {"start": v(-23.09, 2.31) * mm, "end": v(-27.71, 2.31) * mm});
            skLineSegment(sketch, "E3.6.8.1", {"start": v(-23.09, -2.31) * mm, "end": v(-23.09, 2.31) * mm});
            skLineSegment(sketch, "E3.6.8.2", {"start": v(-23.09, -2.31) * mm, "end": v(-27.71, -2.31) * mm});
            skLineSegment(sketch, "E3.6.8.3", {"start": v(-27.71, -2.31) * mm, "end": v(-27.71, 2.31) * mm});
            skLineSegment(sketch, "E3.6.9.0", {"start": v(-23.09, 15.01) * mm, "end": v(-27.71, 15.01) * mm});
            skLineSegment(sketch, "E3.6.9.1", {"start": v(-23.09, 10.39) * mm, "end": v(-23.09, 15.01) * mm});
            skLineSegment(sketch, "E3.6.9.2", {"start": v(-23.09, 10.39) * mm, "end": v(-27.71, 10.39) * mm});
            skLineSegment(sketch, "E3.6.9.3", {"start": v(-27.71, 10.39) * mm, "end": v(-27.71, 15.01) * mm});
            skLineSegment(sketch, "E3.6.10.0", {"start": v(-23.09, 27.71) * mm, "end": v(-27.71, 27.71) * mm});
            skLineSegment(sketch, "E3.6.10.1", {"start": v(-23.09, 23.09) * mm, "end": v(-23.09, 27.71) * mm});
            skLineSegment(sketch, "E3.6.10.2", {"start": v(-23.09, 23.09) * mm, "end": v(-27.71, 23.09) * mm});
            skLineSegment(sketch, "E3.6.10.3", {"start": v(-27.71, 23.09) * mm, "end": v(-27.71, 27.71) * mm});
            skLineSegment(sketch, "E3.6.11.0", {"start": v(-23.09, 40.41) * mm, "end": v(-27.71, 40.41) * mm});
            skLineSegment(sketch, "E3.6.11.1", {"start": v(-23.09, 35.79) * mm, "end": v(-23.09, 40.41) * mm});
            skLineSegment(sketch, "E3.6.11.2", {"start": v(-23.09, 35.79) * mm, "end": v(-27.71, 35.79) * mm});
            skLineSegment(sketch, "E3.6.11.3", {"start": v(-27.71, 35.79) * mm, "end": v(-27.71, 40.41) * mm});
            skLineSegment(sketch, "E3.6.12.0", {"start": v(-23.09, 53.11) * mm, "end": v(-27.71, 53.11) * mm});
            skLineSegment(sketch, "E3.6.12.1", {"start": v(-23.09, 48.49) * mm, "end": v(-23.09, 53.11) * mm});
            skLineSegment(sketch, "E3.6.12.2", {"start": v(-23.09, 48.49) * mm, "end": v(-27.71, 48.49) * mm});
            skLineSegment(sketch, "E3.6.12.3", {"start": v(-27.71, 48.49) * mm, "end": v(-27.71, 53.11) * mm});
            skLineSegment(sketch, "E3.6.13.0", {"start": v(-23.09, 65.81) * mm, "end": v(-27.71, 65.81) * mm});
            skLineSegment(sketch, "E3.6.13.1", {"start": v(-23.09, 61.19) * mm, "end": v(-23.09, 65.81) * mm});
            skLineSegment(sketch, "E3.6.13.2", {"start": v(-23.09, 61.19) * mm, "end": v(-27.71, 61.19) * mm});
            skLineSegment(sketch, "E3.6.13.3", {"start": v(-27.71, 61.19) * mm, "end": v(-27.71, 65.81) * mm});
            skLineSegment(sketch, "E3.6.14.0", {"start": v(-23.09, 78.51) * mm, "end": v(-27.71, 78.51) * mm});
            skLineSegment(sketch, "E3.6.14.1", {"start": v(-23.09, 73.89) * mm, "end": v(-23.09, 78.51) * mm});
            skLineSegment(sketch, "E3.6.14.2", {"start": v(-23.09, 73.89) * mm, "end": v(-27.71, 73.89) * mm});
            skLineSegment(sketch, "E3.6.14.3", {"start": v(-27.71, 73.89) * mm, "end": v(-27.71, 78.51) * mm});
            skLineSegment(sketch, "E3.6.15.0", {"start": v(-23.09, 91.21) * mm, "end": v(-27.71, 91.21) * mm});
            skLineSegment(sketch, "E3.6.15.1", {"start": v(-23.09, 86.59) * mm, "end": v(-23.09, 91.21) * mm});
            skLineSegment(sketch, "E3.6.15.2", {"start": v(-23.09, 86.59) * mm, "end": v(-27.71, 86.59) * mm});
            skLineSegment(sketch, "E3.6.15.3", {"start": v(-27.71, 86.59) * mm, "end": v(-27.71, 91.21) * mm});
            skLineSegment(sketch, "E3.6.16.0", {"start": v(-23.09, 103.91) * mm, "end": v(-27.71, 103.91) * mm});
            skLineSegment(sketch, "E3.6.16.1", {"start": v(-23.09, 99.29) * mm, "end": v(-23.09, 103.91) * mm});
            skLineSegment(sketch, "E3.6.16.2", {"start": v(-23.09, 99.29) * mm, "end": v(-27.71, 99.29) * mm});
            skLineSegment(sketch, "E3.6.16.3", {"start": v(-27.71, 99.29) * mm, "end": v(-27.71, 103.91) * mm});
            skLineSegment(sketch, "E3.7.0.0", {"start": v(-10.39, -99.29) * mm, "end": v(-15.01, -99.29) * mm});
            skLineSegment(sketch, "E3.7.0.1", {"start": v(-10.39, -103.91) * mm, "end": v(-10.39, -99.29) * mm});
            skLineSegment(sketch, "E3.7.0.2", {"start": v(-10.39, -103.91) * mm, "end": v(-15.01, -103.91) * mm});
            skLineSegment(sketch, "E3.7.0.3", {"start": v(-15.01, -103.91) * mm, "end": v(-15.01, -99.29) * mm});
            skLineSegment(sketch, "E3.7.1.0", {"start": v(-10.39, -86.59) * mm, "end": v(-15.01, -86.59) * mm});
            skLineSegment(sketch, "E3.7.1.1", {"start": v(-10.39, -91.21) * mm, "end": v(-10.39, -86.59) * mm});
            skLineSegment(sketch, "E3.7.1.2", {"start": v(-10.39, -91.21) * mm, "end": v(-15.01, -91.21) * mm});
            skLineSegment(sketch, "E3.7.1.3", {"start": v(-15.01, -91.21) * mm, "end": v(-15.01, -86.59) * mm});
            skLineSegment(sketch, "E3.7.2.0", {"start": v(-10.39, -73.89) * mm, "end": v(-15.01, -73.89) * mm});
            skLineSegment(sketch, "E3.7.2.1", {"start": v(-10.39, -78.51) * mm, "end": v(-10.39, -73.89) * mm});
            skLineSegment(sketch, "E3.7.2.2", {"start": v(-10.39, -78.51) * mm, "end": v(-15.01, -78.51) * mm});
            skLineSegment(sketch, "E3.7.2.3", {"start": v(-15.01, -78.51) * mm, "end": v(-15.01, -73.89) * mm});
            skLineSegment(sketch, "E3.7.3.0", {"start": v(-10.39, -61.19) * mm, "end": v(-15.01, -61.19) * mm});
            skLineSegment(sketch, "E3.7.3.1", {"start": v(-10.39, -65.81) * mm, "end": v(-10.39, -61.19) * mm});
            skLineSegment(sketch, "E3.7.3.2", {"start": v(-10.39, -65.81) * mm, "end": v(-15.01, -65.81) * mm});
            skLineSegment(sketch, "E3.7.3.3", {"start": v(-15.01, -65.81) * mm, "end": v(-15.01, -61.19) * mm});
            skLineSegment(sketch, "E3.7.4.0", {"start": v(-10.39, -48.49) * mm, "end": v(-15.01, -48.49) * mm});
            skLineSegment(sketch, "E3.7.4.1", {"start": v(-10.39, -53.11) * mm, "end": v(-10.39, -48.49) * mm});
            skLineSegment(sketch, "E3.7.4.2", {"start": v(-10.39, -53.11) * mm, "end": v(-15.01, -53.11) * mm});
            skLineSegment(sketch, "E3.7.4.3", {"start": v(-15.01, -53.11) * mm, "end": v(-15.01, -48.49) * mm});
            skLineSegment(sketch, "E3.7.5.0", {"start": v(-10.39, -35.79) * mm, "end": v(-15.01, -35.79) * mm});
            skLineSegment(sketch, "E3.7.5.1", {"start": v(-10.39, -40.41) * mm, "end": v(-10.39, -35.79) * mm});
            skLineSegment(sketch, "E3.7.5.2", {"start": v(-10.39, -40.41) * mm, "end": v(-15.01, -40.41) * mm});
            skLineSegment(sketch, "E3.7.5.3", {"start": v(-15.01, -40.41) * mm, "end": v(-15.01, -35.79) * mm});
            skLineSegment(sketch, "E3.7.6.0", {"start": v(-10.39, -23.09) * mm, "end": v(-15.01, -23.09) * mm});
            skLineSegment(sketch, "E3.7.6.1", {"start": v(-10.39, -27.71) * mm, "end": v(-10.39, -23.09) * mm});
            skLineSegment(sketch, "E3.7.6.2", {"start": v(-10.39, -27.71) * mm, "end": v(-15.01, -27.71) * mm});
            skLineSegment(sketch, "E3.7.6.3", {"start": v(-15.01, -27.71) * mm, "end": v(-15.01, -23.09) * mm});
            skLineSegment(sketch, "E3.7.7.0", {"start": v(-10.39, -10.39) * mm, "end": v(-15.01, -10.39) * mm});
            skLineSegment(sketch, "E3.7.7.1", {"start": v(-10.39, -15.01) * mm, "end": v(-10.39, -10.39) * mm});
            skLineSegment(sketch, "E3.7.7.2", {"start": v(-10.39, -15.01) * mm, "end": v(-15.01, -15.01) * mm});
            skLineSegment(sketch, "E3.7.7.3", {"start": v(-15.01, -15.01) * mm, "end": v(-15.01, -10.39) * mm});
            skLineSegment(sketch, "E3.7.8.0", {"start": v(-10.39, 2.31) * mm, "end": v(-15.01, 2.31) * mm});
            skLineSegment(sketch, "E3.7.8.1", {"start": v(-10.39, -2.31) * mm, "end": v(-10.39, 2.31) * mm});
            skLineSegment(sketch, "E3.7.8.2", {"start": v(-10.39, -2.31) * mm, "end": v(-15.01, -2.31) * mm});
            skLineSegment(sketch, "E3.7.8.3", {"start": v(-15.01, -2.31) * mm, "end": v(-15.01, 2.31) * mm});
            skLineSegment(sketch, "E3.7.9.0", {"start": v(-10.39, 15.01) * mm, "end": v(-15.01, 15.01) * mm});
            skLineSegment(sketch, "E3.7.9.1", {"start": v(-10.39, 10.39) * mm, "end": v(-10.39, 15.01) * mm});
            skLineSegment(sketch, "E3.7.9.2", {"start": v(-10.39, 10.39) * mm, "end": v(-15.01, 10.39) * mm});
            skLineSegment(sketch, "E3.7.9.3", {"start": v(-15.01, 10.39) * mm, "end": v(-15.01, 15.01) * mm});
            skLineSegment(sketch, "E3.7.10.0", {"start": v(-10.39, 27.71) * mm, "end": v(-15.01, 27.71) * mm});
            skLineSegment(sketch, "E3.7.10.1", {"start": v(-10.39, 23.09) * mm, "end": v(-10.39, 27.71) * mm});
            skLineSegment(sketch, "E3.7.10.2", {"start": v(-10.39, 23.09) * mm, "end": v(-15.01, 23.09) * mm});
            skLineSegment(sketch, "E3.7.10.3", {"start": v(-15.01, 23.09) * mm, "end": v(-15.01, 27.71) * mm});
            skLineSegment(sketch, "E3.7.11.0", {"start": v(-10.39, 40.41) * mm, "end": v(-15.01, 40.41) * mm});
            skLineSegment(sketch, "E3.7.11.1", {"start": v(-10.39, 35.79) * mm, "end": v(-10.39, 40.41) * mm});
            skLineSegment(sketch, "E3.7.11.2", {"start": v(-10.39, 35.79) * mm, "end": v(-15.01, 35.79) * mm});
            skLineSegment(sketch, "E3.7.11.3", {"start": v(-15.01, 35.79) * mm, "end": v(-15.01, 40.41) * mm});
            skLineSegment(sketch, "E3.7.12.0", {"start": v(-10.39, 53.11) * mm, "end": v(-15.01, 53.11) * mm});
            skLineSegment(sketch, "E3.7.12.1", {"start": v(-10.39, 48.49) * mm, "end": v(-10.39, 53.11) * mm});
            skLineSegment(sketch, "E3.7.12.2", {"start": v(-10.39, 48.49) * mm, "end": v(-15.01, 48.49) * mm});
            skLineSegment(sketch, "E3.7.12.3", {"start": v(-15.01, 48.49) * mm, "end": v(-15.01, 53.11) * mm});
            skLineSegment(sketch, "E3.7.13.0", {"start": v(-10.39, 65.81) * mm, "end": v(-15.01, 65.81) * mm});
            skLineSegment(sketch, "E3.7.13.1", {"start": v(-10.39, 61.19) * mm, "end": v(-10.39, 65.81) * mm});
            skLineSegment(sketch, "E3.7.13.2", {"start": v(-10.39, 61.19) * mm, "end": v(-15.01, 61.19) * mm});
            skLineSegment(sketch, "E3.7.13.3", {"start": v(-15.01, 61.19) * mm, "end": v(-15.01, 65.81) * mm});
            skLineSegment(sketch, "E3.7.14.0", {"start": v(-10.39, 78.51) * mm, "end": v(-15.01, 78.51) * mm});
            skLineSegment(sketch, "E3.7.14.1", {"start": v(-10.39, 73.89) * mm, "end": v(-10.39, 78.51) * mm});
            skLineSegment(sketch, "E3.7.14.2", {"start": v(-10.39, 73.89) * mm, "end": v(-15.01, 73.89) * mm});
            skLineSegment(sketch, "E3.7.14.3", {"start": v(-15.01, 73.89) * mm, "end": v(-15.01, 78.51) * mm});
            skLineSegment(sketch, "E3.7.15.0", {"start": v(-10.39, 91.21) * mm, "end": v(-15.01, 91.21) * mm});
            skLineSegment(sketch, "E3.7.15.1", {"start": v(-10.39, 86.59) * mm, "end": v(-10.39, 91.21) * mm});
            skLineSegment(sketch, "E3.7.15.2", {"start": v(-10.39, 86.59) * mm, "end": v(-15.01, 86.59) * mm});
            skLineSegment(sketch, "E3.7.15.3", {"start": v(-15.01, 86.59) * mm, "end": v(-15.01, 91.21) * mm});
            skLineSegment(sketch, "E3.7.16.0", {"start": v(-10.39, 103.91) * mm, "end": v(-15.01, 103.91) * mm});
            skLineSegment(sketch, "E3.7.16.1", {"start": v(-10.39, 99.29) * mm, "end": v(-10.39, 103.91) * mm});
            skLineSegment(sketch, "E3.7.16.2", {"start": v(-10.39, 99.29) * mm, "end": v(-15.01, 99.29) * mm});
            skLineSegment(sketch, "E3.7.16.3", {"start": v(-15.01, 99.29) * mm, "end": v(-15.01, 103.91) * mm});
            skLineSegment(sketch, "E3.8.0.0", {"start": v(2.31, -99.29) * mm, "end": v(-2.31, -99.29) * mm});
            skLineSegment(sketch, "E3.8.0.1", {"start": v(2.31, -103.91) * mm, "end": v(2.31, -99.29) * mm});
            skLineSegment(sketch, "E3.8.0.2", {"start": v(2.31, -103.91) * mm, "end": v(-2.31, -103.91) * mm});
            skLineSegment(sketch, "E3.8.0.3", {"start": v(-2.31, -103.91) * mm, "end": v(-2.31, -99.29) * mm});
            skLineSegment(sketch, "E3.8.1.0", {"start": v(2.31, -86.59) * mm, "end": v(-2.31, -86.59) * mm});
            skLineSegment(sketch, "E3.8.1.1", {"start": v(2.31, -91.21) * mm, "end": v(2.31, -86.59) * mm});
            skLineSegment(sketch, "E3.8.1.2", {"start": v(2.31, -91.21) * mm, "end": v(-2.31, -91.21) * mm});
            skLineSegment(sketch, "E3.8.1.3", {"start": v(-2.31, -91.21) * mm, "end": v(-2.31, -86.59) * mm});
            skLineSegment(sketch, "E3.8.2.0", {"start": v(2.31, -73.89) * mm, "end": v(-2.31, -73.89) * mm});
            skLineSegment(sketch, "E3.8.2.1", {"start": v(2.31, -78.51) * mm, "end": v(2.31, -73.89) * mm});
            skLineSegment(sketch, "E3.8.2.2", {"start": v(2.31, -78.51) * mm, "end": v(-2.31, -78.51) * mm});
            skLineSegment(sketch, "E3.8.2.3", {"start": v(-2.31, -78.51) * mm, "end": v(-2.31, -73.89) * mm});
            skLineSegment(sketch, "E3.8.3.0", {"start": v(2.31, -61.19) * mm, "end": v(-2.31, -61.19) * mm});
            skLineSegment(sketch, "E3.8.3.1", {"start": v(2.31, -65.81) * mm, "end": v(2.31, -61.19) * mm});
            skLineSegment(sketch, "E3.8.3.2", {"start": v(2.31, -65.81) * mm, "end": v(-2.31, -65.81) * mm});
            skLineSegment(sketch, "E3.8.3.3", {"start": v(-2.31, -65.81) * mm, "end": v(-2.31, -61.19) * mm});
            skLineSegment(sketch, "E3.8.4.0", {"start": v(2.31, -48.49) * mm, "end": v(-2.31, -48.49) * mm});
            skLineSegment(sketch, "E3.8.4.1", {"start": v(2.31, -53.11) * mm, "end": v(2.31, -48.49) * mm});
            skLineSegment(sketch, "E3.8.4.2", {"start": v(2.31, -53.11) * mm, "end": v(-2.31, -53.11) * mm});
            skLineSegment(sketch, "E3.8.4.3", {"start": v(-2.31, -53.11) * mm, "end": v(-2.31, -48.49) * mm});
            skLineSegment(sketch, "E3.8.5.0", {"start": v(2.31, -35.79) * mm, "end": v(-2.31, -35.79) * mm});
            skLineSegment(sketch, "E3.8.5.1", {"start": v(2.31, -40.41) * mm, "end": v(2.31, -35.79) * mm});
            skLineSegment(sketch, "E3.8.5.2", {"start": v(2.31, -40.41) * mm, "end": v(-2.31, -40.41) * mm});
            skLineSegment(sketch, "E3.8.5.3", {"start": v(-2.31, -40.41) * mm, "end": v(-2.31, -35.79) * mm});
            skLineSegment(sketch, "E3.8.6.0", {"start": v(2.31, -23.09) * mm, "end": v(-2.31, -23.09) * mm});
            skLineSegment(sketch, "E3.8.6.1", {"start": v(2.31, -27.71) * mm, "end": v(2.31, -23.09) * mm});
            skLineSegment(sketch, "E3.8.6.2", {"start": v(2.31, -27.71) * mm, "end": v(-2.31, -27.71) * mm});
            skLineSegment(sketch, "E3.8.6.3", {"start": v(-2.31, -27.71) * mm, "end": v(-2.31, -23.09) * mm});
            skLineSegment(sketch, "E3.8.7.0", {"start": v(2.31, -10.39) * mm, "end": v(-2.31, -10.39) * mm});
            skLineSegment(sketch, "E3.8.7.1", {"start": v(2.31, -15.01) * mm, "end": v(2.31, -10.39) * mm});
            skLineSegment(sketch, "E3.8.7.2", {"start": v(2.31, -15.01) * mm, "end": v(-2.31, -15.01) * mm});
            skLineSegment(sketch, "E3.8.7.3", {"start": v(-2.31, -15.01) * mm, "end": v(-2.31, -10.39) * mm});
            skLineSegment(sketch, "E3.8.8.0", {"start": v(2.31, 2.31) * mm, "end": v(-2.31, 2.31) * mm});
            skLineSegment(sketch, "E3.8.8.1", {"start": v(2.31, -2.31) * mm, "end": v(2.31, 2.31) * mm});
            skLineSegment(sketch, "E3.8.8.2", {"start": v(2.31, -2.31) * mm, "end": v(-2.31, -2.31) * mm});
            skLineSegment(sketch, "E3.8.8.3", {"start": v(-2.31, -2.31) * mm, "end": v(-2.31, 2.31) * mm});
            skLineSegment(sketch, "E3.8.9.0", {"start": v(2.31, 15.01) * mm, "end": v(-2.31, 15.01) * mm});
            skLineSegment(sketch, "E3.8.9.1", {"start": v(2.31, 10.39) * mm, "end": v(2.31, 15.01) * mm});
            skLineSegment(sketch, "E3.8.9.2", {"start": v(2.31, 10.39) * mm, "end": v(-2.31, 10.39) * mm});
            skLineSegment(sketch, "E3.8.9.3", {"start": v(-2.31, 10.39) * mm, "end": v(-2.31, 15.01) * mm});
            skLineSegment(sketch, "E3.8.10.0", {"start": v(2.31, 27.71) * mm, "end": v(-2.31, 27.71) * mm});
            skLineSegment(sketch, "E3.8.10.1", {"start": v(2.31, 23.09) * mm, "end": v(2.31, 27.71) * mm});
            skLineSegment(sketch, "E3.8.10.2", {"start": v(2.31, 23.09) * mm, "end": v(-2.31, 23.09) * mm});
            skLineSegment(sketch, "E3.8.10.3", {"start": v(-2.31, 23.09) * mm, "end": v(-2.31, 27.71) * mm});
            skLineSegment(sketch, "E3.8.11.0", {"start": v(2.31, 40.41) * mm, "end": v(-2.31, 40.41) * mm});
            skLineSegment(sketch, "E3.8.11.1", {"start": v(2.31, 35.79) * mm, "end": v(2.31, 40.41) * mm});
            skLineSegment(sketch, "E3.8.11.2", {"start": v(2.31, 35.79) * mm, "end": v(-2.31, 35.79) * mm});
            skLineSegment(sketch, "E3.8.11.3", {"start": v(-2.31, 35.79) * mm, "end": v(-2.31, 40.41) * mm});
            skLineSegment(sketch, "E3.8.12.0", {"start": v(2.31, 53.11) * mm, "end": v(-2.31, 53.11) * mm});
            skLineSegment(sketch, "E3.8.12.1", {"start": v(2.31, 48.49) * mm, "end": v(2.31, 53.11) * mm});
            skLineSegment(sketch, "E3.8.12.2", {"start": v(2.31, 48.49) * mm, "end": v(-2.31, 48.49) * mm});
            skLineSegment(sketch, "E3.8.12.3", {"start": v(-2.31, 48.49) * mm, "end": v(-2.31, 53.11) * mm});
            skLineSegment(sketch, "E3.8.13.0", {"start": v(2.31, 65.81) * mm, "end": v(-2.31, 65.81) * mm});
            skLineSegment(sketch, "E3.8.13.1", {"start": v(2.31, 61.19) * mm, "end": v(2.31, 65.81) * mm});
            skLineSegment(sketch, "E3.8.13.2", {"start": v(2.31, 61.19) * mm, "end": v(-2.31, 61.19) * mm});
            skLineSegment(sketch, "E3.8.13.3", {"start": v(-2.31, 61.19) * mm, "end": v(-2.31, 65.81) * mm});
            skLineSegment(sketch, "E3.8.14.0", {"start": v(2.31, 78.51) * mm, "end": v(-2.31, 78.51) * mm});
            skLineSegment(sketch, "E3.8.14.1", {"start": v(2.31, 73.89) * mm, "end": v(2.31, 78.51) * mm});
            skLineSegment(sketch, "E3.8.14.2", {"start": v(2.31, 73.89) * mm, "end": v(-2.31, 73.89) * mm});
            skLineSegment(sketch, "E3.8.14.3", {"start": v(-2.31, 73.89) * mm, "end": v(-2.31, 78.51) * mm});
            skLineSegment(sketch, "E3.8.15.0", {"start": v(2.31, 91.21) * mm, "end": v(-2.31, 91.21) * mm});
            skLineSegment(sketch, "E3.8.15.1", {"start": v(2.31, 86.59) * mm, "end": v(2.31, 91.21) * mm});
            skLineSegment(sketch, "E3.8.15.2", {"start": v(2.31, 86.59) * mm, "end": v(-2.31, 86.59) * mm});
            skLineSegment(sketch, "E3.8.15.3", {"start": v(-2.31, 86.59) * mm, "end": v(-2.31, 91.21) * mm});
            skLineSegment(sketch, "E3.8.16.0", {"start": v(2.31, 103.91) * mm, "end": v(-2.31, 103.91) * mm});
            skLineSegment(sketch, "E3.8.16.1", {"start": v(2.31, 99.29) * mm, "end": v(2.31, 103.91) * mm});
            skLineSegment(sketch, "E3.8.16.2", {"start": v(2.31, 99.29) * mm, "end": v(-2.31, 99.29) * mm});
            skLineSegment(sketch, "E3.8.16.3", {"start": v(-2.31, 99.29) * mm, "end": v(-2.31, 103.91) * mm});
            skLineSegment(sketch, "E3.9.0.0", {"start": v(15.01, -99.29) * mm, "end": v(10.39, -99.29) * mm});
            skLineSegment(sketch, "E3.9.0.1", {"start": v(15.01, -103.91) * mm, "end": v(15.01, -99.29) * mm});
            skLineSegment(sketch, "E3.9.0.2", {"start": v(15.01, -103.91) * mm, "end": v(10.39, -103.91) * mm});
            skLineSegment(sketch, "E3.9.0.3", {"start": v(10.39, -103.91) * mm, "end": v(10.39, -99.29) * mm});
            skLineSegment(sketch, "E3.9.1.0", {"start": v(15.01, -86.59) * mm, "end": v(10.39, -86.59) * mm});
            skLineSegment(sketch, "E3.9.1.1", {"start": v(15.01, -91.21) * mm, "end": v(15.01, -86.59) * mm});
            skLineSegment(sketch, "E3.9.1.2", {"start": v(15.01, -91.21) * mm, "end": v(10.39, -91.21) * mm});
            skLineSegment(sketch, "E3.9.1.3", {"start": v(10.39, -91.21) * mm, "end": v(10.39, -86.59) * mm});
            skLineSegment(sketch, "E3.9.2.0", {"start": v(15.01, -73.89) * mm, "end": v(10.39, -73.89) * mm});
            skLineSegment(sketch, "E3.9.2.1", {"start": v(15.01, -78.51) * mm, "end": v(15.01, -73.89) * mm});
            skLineSegment(sketch, "E3.9.2.2", {"start": v(15.01, -78.51) * mm, "end": v(10.39, -78.51) * mm});
            skLineSegment(sketch, "E3.9.2.3", {"start": v(10.39, -78.51) * mm, "end": v(10.39, -73.89) * mm});
            skLineSegment(sketch, "E3.9.3.0", {"start": v(15.01, -61.19) * mm, "end": v(10.39, -61.19) * mm});
            skLineSegment(sketch, "E3.9.3.1", {"start": v(15.01, -65.81) * mm, "end": v(15.01, -61.19) * mm});
            skLineSegment(sketch, "E3.9.3.2", {"start": v(15.01, -65.81) * mm, "end": v(10.39, -65.81) * mm});
            skLineSegment(sketch, "E3.9.3.3", {"start": v(10.39, -65.81) * mm, "end": v(10.39, -61.19) * mm});
            skLineSegment(sketch, "E3.9.4.0", {"start": v(15.01, -48.49) * mm, "end": v(10.39, -48.49) * mm});
            skLineSegment(sketch, "E3.9.4.1", {"start": v(15.01, -53.11) * mm, "end": v(15.01, -48.49) * mm});
            skLineSegment(sketch, "E3.9.4.2", {"start": v(15.01, -53.11) * mm, "end": v(10.39, -53.11) * mm});
            skLineSegment(sketch, "E3.9.4.3", {"start": v(10.39, -53.11) * mm, "end": v(10.39, -48.49) * mm});
            skLineSegment(sketch, "E3.9.5.0", {"start": v(15.01, -35.79) * mm, "end": v(10.39, -35.79) * mm});
            skLineSegment(sketch, "E3.9.5.1", {"start": v(15.01, -40.41) * mm, "end": v(15.01, -35.79) * mm});
            skLineSegment(sketch, "E3.9.5.2", {"start": v(15.01, -40.41) * mm, "end": v(10.39, -40.41) * mm});
            skLineSegment(sketch, "E3.9.5.3", {"start": v(10.39, -40.41) * mm, "end": v(10.39, -35.79) * mm});
            skLineSegment(sketch, "E3.9.6.0", {"start": v(15.01, -23.09) * mm, "end": v(10.39, -23.09) * mm});
            skLineSegment(sketch, "E3.9.6.1", {"start": v(15.01, -27.71) * mm, "end": v(15.01, -23.09) * mm});
            skLineSegment(sketch, "E3.9.6.2", {"start": v(15.01, -27.71) * mm, "end": v(10.39, -27.71) * mm});
            skLineSegment(sketch, "E3.9.6.3", {"start": v(10.39, -27.71) * mm, "end": v(10.39, -23.09) * mm});
            skLineSegment(sketch, "E3.9.7.0", {"start": v(15.01, -10.39) * mm, "end": v(10.39, -10.39) * mm});
            skLineSegment(sketch, "E3.9.7.1", {"start": v(15.01, -15.01) * mm, "end": v(15.01, -10.39) * mm});
            skLineSegment(sketch, "E3.9.7.2", {"start": v(15.01, -15.01) * mm, "end": v(10.39, -15.01) * mm});
            skLineSegment(sketch, "E3.9.7.3", {"start": v(10.39, -15.01) * mm, "end": v(10.39, -10.39) * mm});
            skLineSegment(sketch, "E3.9.8.0", {"start": v(15.01, 2.31) * mm, "end": v(10.39, 2.31) * mm});
            skLineSegment(sketch, "E3.9.8.1", {"start": v(15.01, -2.31) * mm, "end": v(15.01, 2.31) * mm});
            skLineSegment(sketch, "E3.9.8.2", {"start": v(15.01, -2.31) * mm, "end": v(10.39, -2.31) * mm});
            skLineSegment(sketch, "E3.9.8.3", {"start": v(10.39, -2.31) * mm, "end": v(10.39, 2.31) * mm});
            skLineSegment(sketch, "E3.9.9.0", {"start": v(15.01, 15.01) * mm, "end": v(10.39, 15.01) * mm});
            skLineSegment(sketch, "E3.9.9.1", {"start": v(15.01, 10.39) * mm, "end": v(15.01, 15.01) * mm});
            skLineSegment(sketch, "E3.9.9.2", {"start": v(15.01, 10.39) * mm, "end": v(10.39, 10.39) * mm});
            skLineSegment(sketch, "E3.9.9.3", {"start": v(10.39, 10.39) * mm, "end": v(10.39, 15.01) * mm});
            skLineSegment(sketch, "E3.9.10.0", {"start": v(15.01, 27.71) * mm, "end": v(10.39, 27.71) * mm});
            skLineSegment(sketch, "E3.9.10.1", {"start": v(15.01, 23.09) * mm, "end": v(15.01, 27.71) * mm});
            skLineSegment(sketch, "E3.9.10.2", {"start": v(15.01, 23.09) * mm, "end": v(10.39, 23.09) * mm});
            skLineSegment(sketch, "E3.9.10.3", {"start": v(10.39, 23.09) * mm, "end": v(10.39, 27.71) * mm});
            skLineSegment(sketch, "E3.9.11.0", {"start": v(15.01, 40.41) * mm, "end": v(10.39, 40.41) * mm});
            skLineSegment(sketch, "E3.9.11.1", {"start": v(15.01, 35.79) * mm, "end": v(15.01, 40.41) * mm});
            skLineSegment(sketch, "E3.9.11.2", {"start": v(15.01, 35.79) * mm, "end": v(10.39, 35.79) * mm});
            skLineSegment(sketch, "E3.9.11.3", {"start": v(10.39, 35.79) * mm, "end": v(10.39, 40.41) * mm});
            skLineSegment(sketch, "E3.9.12.0", {"start": v(15.01, 53.11) * mm, "end": v(10.39, 53.11) * mm});
            skLineSegment(sketch, "E3.9.12.1", {"start": v(15.01, 48.49) * mm, "end": v(15.01, 53.11) * mm});
            skLineSegment(sketch, "E3.9.12.2", {"start": v(15.01, 48.49) * mm, "end": v(10.39, 48.49) * mm});
            skLineSegment(sketch, "E3.9.12.3", {"start": v(10.39, 48.49) * mm, "end": v(10.39, 53.11) * mm});
            skLineSegment(sketch, "E3.9.13.0", {"start": v(15.01, 65.81) * mm, "end": v(10.39, 65.81) * mm});
            skLineSegment(sketch, "E3.9.13.1", {"start": v(15.01, 61.19) * mm, "end": v(15.01, 65.81) * mm});
            skLineSegment(sketch, "E3.9.13.2", {"start": v(15.01, 61.19) * mm, "end": v(10.39, 61.19) * mm});
            skLineSegment(sketch, "E3.9.13.3", {"start": v(10.39, 61.19) * mm, "end": v(10.39, 65.81) * mm});
            skLineSegment(sketch, "E3.9.14.0", {"start": v(15.01, 78.51) * mm, "end": v(10.39, 78.51) * mm});
            skLineSegment(sketch, "E3.9.14.1", {"start": v(15.01, 73.89) * mm, "end": v(15.01, 78.51) * mm});
            skLineSegment(sketch, "E3.9.14.2", {"start": v(15.01, 73.89) * mm, "end": v(10.39, 73.89) * mm});
            skLineSegment(sketch, "E3.9.14.3", {"start": v(10.39, 73.89) * mm, "end": v(10.39, 78.51) * mm});
            skLineSegment(sketch, "E3.9.15.0", {"start": v(15.01, 91.21) * mm, "end": v(10.39, 91.21) * mm});
            skLineSegment(sketch, "E3.9.15.1", {"start": v(15.01, 86.59) * mm, "end": v(15.01, 91.21) * mm});
            skLineSegment(sketch, "E3.9.15.2", {"start": v(15.01, 86.59) * mm, "end": v(10.39, 86.59) * mm});
            skLineSegment(sketch, "E3.9.15.3", {"start": v(10.39, 86.59) * mm, "end": v(10.39, 91.21) * mm});
            skLineSegment(sketch, "E3.9.16.0", {"start": v(15.01, 103.91) * mm, "end": v(10.39, 103.91) * mm});
            skLineSegment(sketch, "E3.9.16.1", {"start": v(15.01, 99.29) * mm, "end": v(15.01, 103.91) * mm});
            skLineSegment(sketch, "E3.9.16.2", {"start": v(15.01, 99.29) * mm, "end": v(10.39, 99.29) * mm});
            skLineSegment(sketch, "E3.9.16.3", {"start": v(10.39, 99.29) * mm, "end": v(10.39, 103.91) * mm});
            skLineSegment(sketch, "E3.10.0.0", {"start": v(27.71, -99.29) * mm, "end": v(23.09, -99.29) * mm});
            skLineSegment(sketch, "E3.10.0.1", {"start": v(27.71, -103.91) * mm, "end": v(27.71, -99.29) * mm});
            skLineSegment(sketch, "E3.10.0.2", {"start": v(27.71, -103.91) * mm, "end": v(23.09, -103.91) * mm});
            skLineSegment(sketch, "E3.10.0.3", {"start": v(23.09, -103.91) * mm, "end": v(23.09, -99.29) * mm});
            skLineSegment(sketch, "E3.10.1.0", {"start": v(27.71, -86.59) * mm, "end": v(23.09, -86.59) * mm});
            skLineSegment(sketch, "E3.10.1.1", {"start": v(27.71, -91.21) * mm, "end": v(27.71, -86.59) * mm});
            skLineSegment(sketch, "E3.10.1.2", {"start": v(27.71, -91.21) * mm, "end": v(23.09, -91.21) * mm});
            skLineSegment(sketch, "E3.10.1.3", {"start": v(23.09, -91.21) * mm, "end": v(23.09, -86.59) * mm});
            skLineSegment(sketch, "E3.10.2.0", {"start": v(27.71, -73.89) * mm, "end": v(23.09, -73.89) * mm});
            skLineSegment(sketch, "E3.10.2.1", {"start": v(27.71, -78.51) * mm, "end": v(27.71, -73.89) * mm});
            skLineSegment(sketch, "E3.10.2.2", {"start": v(27.71, -78.51) * mm, "end": v(23.09, -78.51) * mm});
            skLineSegment(sketch, "E3.10.2.3", {"start": v(23.09, -78.51) * mm, "end": v(23.09, -73.89) * mm});
            skLineSegment(sketch, "E3.10.3.0", {"start": v(27.71, -61.19) * mm, "end": v(23.09, -61.19) * mm});
            skLineSegment(sketch, "E3.10.3.1", {"start": v(27.71, -65.81) * mm, "end": v(27.71, -61.19) * mm});
            skLineSegment(sketch, "E3.10.3.2", {"start": v(27.71, -65.81) * mm, "end": v(23.09, -65.81) * mm});
            skLineSegment(sketch, "E3.10.3.3", {"start": v(23.09, -65.81) * mm, "end": v(23.09, -61.19) * mm});
            skLineSegment(sketch, "E3.10.4.0", {"start": v(27.71, -48.49) * mm, "end": v(23.09, -48.49) * mm});
            skLineSegment(sketch, "E3.10.4.1", {"start": v(27.71, -53.11) * mm, "end": v(27.71, -48.49) * mm});
            skLineSegment(sketch, "E3.10.4.2", {"start": v(27.71, -53.11) * mm, "end": v(23.09, -53.11) * mm});
            skLineSegment(sketch, "E3.10.4.3", {"start": v(23.09, -53.11) * mm, "end": v(23.09, -48.49) * mm});
            skLineSegment(sketch, "E3.10.5.0", {"start": v(27.71, -35.79) * mm, "end": v(23.09, -35.79) * mm});
            skLineSegment(sketch, "E3.10.5.1", {"start": v(27.71, -40.41) * mm, "end": v(27.71, -35.79) * mm});
            skLineSegment(sketch, "E3.10.5.2", {"start": v(27.71, -40.41) * mm, "end": v(23.09, -40.41) * mm});
            skLineSegment(sketch, "E3.10.5.3", {"start": v(23.09, -40.41) * mm, "end": v(23.09, -35.79) * mm});
            skLineSegment(sketch, "E3.10.6.0", {"start": v(27.71, -23.09) * mm, "end": v(23.09, -23.09) * mm});
            skLineSegment(sketch, "E3.10.6.1", {"start": v(27.71, -27.71) * mm, "end": v(27.71, -23.09) * mm});
            skLineSegment(sketch, "E3.10.6.2", {"start": v(27.71, -27.71) * mm, "end": v(23.09, -27.71) * mm});
            skLineSegment(sketch, "E3.10.6.3", {"start": v(23.09, -27.71) * mm, "end": v(23.09, -23.09) * mm});
            skLineSegment(sketch, "E3.10.7.0", {"start": v(27.71, -10.39) * mm, "end": v(23.09, -10.39) * mm});
            skLineSegment(sketch, "E3.10.7.1", {"start": v(27.71, -15.01) * mm, "end": v(27.71, -10.39) * mm});
            skLineSegment(sketch, "E3.10.7.2", {"start": v(27.71, -15.01) * mm, "end": v(23.09, -15.01) * mm});
            skLineSegment(sketch, "E3.10.7.3", {"start": v(23.09, -15.01) * mm, "end": v(23.09, -10.39) * mm});
            skLineSegment(sketch, "E3.10.8.0", {"start": v(27.71, 2.31) * mm, "end": v(23.09, 2.31) * mm});
            skLineSegment(sketch, "E3.10.8.1", {"start": v(27.71, -2.31) * mm, "end": v(27.71, 2.31) * mm});
            skLineSegment(sketch, "E3.10.8.2", {"start": v(27.71, -2.31) * mm, "end": v(23.09, -2.31) * mm});
            skLineSegment(sketch, "E3.10.8.3", {"start": v(23.09, -2.31) * mm, "end": v(23.09, 2.31) * mm});
            skLineSegment(sketch, "E3.10.9.0", {"start": v(27.71, 15.01) * mm, "end": v(23.09, 15.01) * mm});
            skLineSegment(sketch, "E3.10.9.1", {"start": v(27.71, 10.39) * mm, "end": v(27.71, 15.01) * mm});
            skLineSegment(sketch, "E3.10.9.2", {"start": v(27.71, 10.39) * mm, "end": v(23.09, 10.39) * mm});
            skLineSegment(sketch, "E3.10.9.3", {"start": v(23.09, 10.39) * mm, "end": v(23.09, 15.01) * mm});
            skLineSegment(sketch, "E3.10.10.0", {"start": v(27.71, 27.71) * mm, "end": v(23.09, 27.71) * mm});
            skLineSegment(sketch, "E3.10.10.1", {"start": v(27.71, 23.09) * mm, "end": v(27.71, 27.71) * mm});
            skLineSegment(sketch, "E3.10.10.2", {"start": v(27.71, 23.09) * mm, "end": v(23.09, 23.09) * mm});
            skLineSegment(sketch, "E3.10.10.3", {"start": v(23.09, 23.09) * mm, "end": v(23.09, 27.71) * mm});
            skLineSegment(sketch, "E3.10.11.0", {"start": v(27.71, 40.41) * mm, "end": v(23.09, 40.41) * mm});
            skLineSegment(sketch, "E3.10.11.1", {"start": v(27.71, 35.79) * mm, "end": v(27.71, 40.41) * mm});
            skLineSegment(sketch, "E3.10.11.2", {"start": v(27.71, 35.79) * mm, "end": v(23.09, 35.79) * mm});
            skLineSegment(sketch, "E3.10.11.3", {"start": v(23.09, 35.79) * mm, "end": v(23.09, 40.41) * mm});
            skLineSegment(sketch, "E3.10.12.0", {"start": v(27.71, 53.11) * mm, "end": v(23.09, 53.11) * mm});
            skLineSegment(sketch, "E3.10.12.1", {"start": v(27.71, 48.49) * mm, "end": v(27.71, 53.11) * mm});
            skLineSegment(sketch, "E3.10.12.2", {"start": v(27.71, 48.49) * mm, "end": v(23.09, 48.49) * mm});
            skLineSegment(sketch, "E3.10.12.3", {"start": v(23.09, 48.49) * mm, "end": v(23.09, 53.11) * mm});
            skLineSegment(sketch, "E3.10.13.0", {"start": v(27.71, 65.81) * mm, "end": v(23.09, 65.81) * mm});
            skLineSegment(sketch, "E3.10.13.1", {"start": v(27.71, 61.19) * mm, "end": v(27.71, 65.81) * mm});
            skLineSegment(sketch, "E3.10.13.2", {"start": v(27.71, 61.19) * mm, "end": v(23.09, 61.19) * mm});
            skLineSegment(sketch, "E3.10.13.3", {"start": v(23.09, 61.19) * mm, "end": v(23.09, 65.81) * mm});
            skLineSegment(sketch, "E3.10.14.0", {"start": v(27.71, 78.51) * mm, "end": v(23.09, 78.51) * mm});
            skLineSegment(sketch, "E3.10.14.1", {"start": v(27.71, 73.89) * mm, "end": v(27.71, 78.51) * mm});
            skLineSegment(sketch, "E3.10.14.2", {"start": v(27.71, 73.89) * mm, "end": v(23.09, 73.89) * mm});
            skLineSegment(sketch, "E3.10.14.3", {"start": v(23.09, 73.89) * mm, "end": v(23.09, 78.51) * mm});
            skLineSegment(sketch, "E3.10.15.0", {"start": v(27.71, 91.21) * mm, "end": v(23.09, 91.21) * mm});
            skLineSegment(sketch, "E3.10.15.1", {"start": v(27.71, 86.59) * mm, "end": v(27.71, 91.21) * mm});
            skLineSegment(sketch, "E3.10.15.2", {"start": v(27.71, 86.59) * mm, "end": v(23.09, 86.59) * mm});
            skLineSegment(sketch, "E3.10.15.3", {"start": v(23.09, 86.59) * mm, "end": v(23.09, 91.21) * mm});
            skLineSegment(sketch, "E3.10.16.0", {"start": v(27.71, 103.91) * mm, "end": v(23.09, 103.91) * mm});
            skLineSegment(sketch, "E3.10.16.1", {"start": v(27.71, 99.29) * mm, "end": v(27.71, 103.91) * mm});
            skLineSegment(sketch, "E3.10.16.2", {"start": v(27.71, 99.29) * mm, "end": v(23.09, 99.29) * mm});
            skLineSegment(sketch, "E3.10.16.3", {"start": v(23.09, 99.29) * mm, "end": v(23.09, 103.91) * mm});
            skLineSegment(sketch, "E3.11.0.0", {"start": v(40.41, -99.29) * mm, "end": v(35.79, -99.29) * mm});
            skLineSegment(sketch, "E3.11.0.1", {"start": v(40.41, -103.91) * mm, "end": v(40.41, -99.29) * mm});
            skLineSegment(sketch, "E3.11.0.2", {"start": v(40.41, -103.91) * mm, "end": v(35.79, -103.91) * mm});
            skLineSegment(sketch, "E3.11.0.3", {"start": v(35.79, -103.91) * mm, "end": v(35.79, -99.29) * mm});
            skLineSegment(sketch, "E3.11.1.0", {"start": v(40.41, -86.59) * mm, "end": v(35.79, -86.59) * mm});
            skLineSegment(sketch, "E3.11.1.1", {"start": v(40.41, -91.21) * mm, "end": v(40.41, -86.59) * mm});
            skLineSegment(sketch, "E3.11.1.2", {"start": v(40.41, -91.21) * mm, "end": v(35.79, -91.21) * mm});
            skLineSegment(sketch, "E3.11.1.3", {"start": v(35.79, -91.21) * mm, "end": v(35.79, -86.59) * mm});
            skLineSegment(sketch, "E3.11.2.0", {"start": v(40.41, -73.89) * mm, "end": v(35.79, -73.89) * mm});
            skLineSegment(sketch, "E3.11.2.1", {"start": v(40.41, -78.51) * mm, "end": v(40.41, -73.89) * mm});
            skLineSegment(sketch, "E3.11.2.2", {"start": v(40.41, -78.51) * mm, "end": v(35.79, -78.51) * mm});
            skLineSegment(sketch, "E3.11.2.3", {"start": v(35.79, -78.51) * mm, "end": v(35.79, -73.89) * mm});
            skLineSegment(sketch, "E3.11.3.0", {"start": v(40.41, -61.19) * mm, "end": v(35.79, -61.19) * mm});
            skLineSegment(sketch, "E3.11.3.1", {"start": v(40.41, -65.81) * mm, "end": v(40.41, -61.19) * mm});
            skLineSegment(sketch, "E3.11.3.2", {"start": v(40.41, -65.81) * mm, "end": v(35.79, -65.81) * mm});
            skLineSegment(sketch, "E3.11.3.3", {"start": v(35.79, -65.81) * mm, "end": v(35.79, -61.19) * mm});
            skLineSegment(sketch, "E3.11.4.0", {"start": v(40.41, -48.49) * mm, "end": v(35.79, -48.49) * mm});
            skLineSegment(sketch, "E3.11.4.1", {"start": v(40.41, -53.11) * mm, "end": v(40.41, -48.49) * mm});
            skLineSegment(sketch, "E3.11.4.2", {"start": v(40.41, -53.11) * mm, "end": v(35.79, -53.11) * mm});
            skLineSegment(sketch, "E3.11.4.3", {"start": v(35.79, -53.11) * mm, "end": v(35.79, -48.49) * mm});
            skLineSegment(sketch, "E3.11.5.0", {"start": v(40.41, -35.79) * mm, "end": v(35.79, -35.79) * mm});
            skLineSegment(sketch, "E3.11.5.1", {"start": v(40.41, -40.41) * mm, "end": v(40.41, -35.79) * mm});
            skLineSegment(sketch, "E3.11.5.2", {"start": v(40.41, -40.41) * mm, "end": v(35.79, -40.41) * mm});
            skLineSegment(sketch, "E3.11.5.3", {"start": v(35.79, -40.41) * mm, "end": v(35.79, -35.79) * mm});
            skLineSegment(sketch, "E3.11.6.0", {"start": v(40.41, -23.09) * mm, "end": v(35.79, -23.09) * mm});
            skLineSegment(sketch, "E3.11.6.1", {"start": v(40.41, -27.71) * mm, "end": v(40.41, -23.09) * mm});
            skLineSegment(sketch, "E3.11.6.2", {"start": v(40.41, -27.71) * mm, "end": v(35.79, -27.71) * mm});
            skLineSegment(sketch, "E3.11.6.3", {"start": v(35.79, -27.71) * mm, "end": v(35.79, -23.09) * mm});
            skLineSegment(sketch, "E3.11.7.0", {"start": v(40.41, -10.39) * mm, "end": v(35.79, -10.39) * mm});
            skLineSegment(sketch, "E3.11.7.1", {"start": v(40.41, -15.01) * mm, "end": v(40.41, -10.39) * mm});
            skLineSegment(sketch, "E3.11.7.2", {"start": v(40.41, -15.01) * mm, "end": v(35.79, -15.01) * mm});
            skLineSegment(sketch, "E3.11.7.3", {"start": v(35.79, -15.01) * mm, "end": v(35.79, -10.39) * mm});
            skLineSegment(sketch, "E3.11.8.0", {"start": v(40.41, 2.31) * mm, "end": v(35.79, 2.31) * mm});
            skLineSegment(sketch, "E3.11.8.1", {"start": v(40.41, -2.31) * mm, "end": v(40.41, 2.31) * mm});
            skLineSegment(sketch, "E3.11.8.2", {"start": v(40.41, -2.31) * mm, "end": v(35.79, -2.31) * mm});
            skLineSegment(sketch, "E3.11.8.3", {"start": v(35.79, -2.31) * mm, "end": v(35.79, 2.31) * mm});
            skLineSegment(sketch, "E3.11.9.0", {"start": v(40.41, 15.01) * mm, "end": v(35.79, 15.01) * mm});
            skLineSegment(sketch, "E3.11.9.1", {"start": v(40.41, 10.39) * mm, "end": v(40.41, 15.01) * mm});
            skLineSegment(sketch, "E3.11.9.2", {"start": v(40.41, 10.39) * mm, "end": v(35.79, 10.39) * mm});
            skLineSegment(sketch, "E3.11.9.3", {"start": v(35.79, 10.39) * mm, "end": v(35.79, 15.01) * mm});
            skLineSegment(sketch, "E3.11.10.0", {"start": v(40.41, 27.71) * mm, "end": v(35.79, 27.71) * mm});
            skLineSegment(sketch, "E3.11.10.1", {"start": v(40.41, 23.09) * mm, "end": v(40.41, 27.71) * mm});
            skLineSegment(sketch, "E3.11.10.2", {"start": v(40.41, 23.09) * mm, "end": v(35.79, 23.09) * mm});
            skLineSegment(sketch, "E3.11.10.3", {"start": v(35.79, 23.09) * mm, "end": v(35.79, 27.71) * mm});
            skLineSegment(sketch, "E3.11.11.0", {"start": v(40.41, 40.41) * mm, "end": v(35.79, 40.41) * mm});
            skLineSegment(sketch, "E3.11.11.1", {"start": v(40.41, 35.79) * mm, "end": v(40.41, 40.41) * mm});
            skLineSegment(sketch, "E3.11.11.2", {"start": v(40.41, 35.79) * mm, "end": v(35.79, 35.79) * mm});
            skLineSegment(sketch, "E3.11.11.3", {"start": v(35.79, 35.79) * mm, "end": v(35.79, 40.41) * mm});
            skLineSegment(sketch, "E3.11.12.0", {"start": v(40.41, 53.11) * mm, "end": v(35.79, 53.11) * mm});
            skLineSegment(sketch, "E3.11.12.1", {"start": v(40.41, 48.49) * mm, "end": v(40.41, 53.11) * mm});
            skLineSegment(sketch, "E3.11.12.2", {"start": v(40.41, 48.49) * mm, "end": v(35.79, 48.49) * mm});
            skLineSegment(sketch, "E3.11.12.3", {"start": v(35.79, 48.49) * mm, "end": v(35.79, 53.11) * mm});
            skLineSegment(sketch, "E3.11.13.0", {"start": v(40.41, 65.81) * mm, "end": v(35.79, 65.81) * mm});
            skLineSegment(sketch, "E3.11.13.1", {"start": v(40.41, 61.19) * mm, "end": v(40.41, 65.81) * mm});
            skLineSegment(sketch, "E3.11.13.2", {"start": v(40.41, 61.19) * mm, "end": v(35.79, 61.19) * mm});
            skLineSegment(sketch, "E3.11.13.3", {"start": v(35.79, 61.19) * mm, "end": v(35.79, 65.81) * mm});
            skLineSegment(sketch, "E3.11.14.0", {"start": v(40.41, 78.51) * mm, "end": v(35.79, 78.51) * mm});
            skLineSegment(sketch, "E3.11.14.1", {"start": v(40.41, 73.89) * mm, "end": v(40.41, 78.51) * mm});
            skLineSegment(sketch, "E3.11.14.2", {"start": v(40.41, 73.89) * mm, "end": v(35.79, 73.89) * mm});
            skLineSegment(sketch, "E3.11.14.3", {"start": v(35.79, 73.89) * mm, "end": v(35.79, 78.51) * mm});
            skLineSegment(sketch, "E3.11.15.0", {"start": v(40.41, 91.21) * mm, "end": v(35.79, 91.21) * mm});
            skLineSegment(sketch, "E3.11.15.1", {"start": v(40.41, 86.59) * mm, "end": v(40.41, 91.21) * mm});
            skLineSegment(sketch, "E3.11.15.2", {"start": v(40.41, 86.59) * mm, "end": v(35.79, 86.59) * mm});
            skLineSegment(sketch, "E3.11.15.3", {"start": v(35.79, 86.59) * mm, "end": v(35.79, 91.21) * mm});
            skLineSegment(sketch, "E3.11.16.0", {"start": v(40.41, 103.91) * mm, "end": v(35.79, 103.91) * mm});
            skLineSegment(sketch, "E3.11.16.1", {"start": v(40.41, 99.29) * mm, "end": v(40.41, 103.91) * mm});
            skLineSegment(sketch, "E3.11.16.2", {"start": v(40.41, 99.29) * mm, "end": v(35.79, 99.29) * mm});
            skLineSegment(sketch, "E3.11.16.3", {"start": v(35.79, 99.29) * mm, "end": v(35.79, 103.91) * mm});
            skLineSegment(sketch, "E3.12.0.0", {"start": v(53.11, -99.29) * mm, "end": v(48.49, -99.29) * mm});
            skLineSegment(sketch, "E3.12.0.1", {"start": v(53.11, -103.91) * mm, "end": v(53.11, -99.29) * mm});
            skLineSegment(sketch, "E3.12.0.2", {"start": v(53.11, -103.91) * mm, "end": v(48.49, -103.91) * mm});
            skLineSegment(sketch, "E3.12.0.3", {"start": v(48.49, -103.91) * mm, "end": v(48.49, -99.29) * mm});
            skLineSegment(sketch, "E3.12.1.0", {"start": v(53.11, -86.59) * mm, "end": v(48.49, -86.59) * mm});
            skLineSegment(sketch, "E3.12.1.1", {"start": v(53.11, -91.21) * mm, "end": v(53.11, -86.59) * mm});
            skLineSegment(sketch, "E3.12.1.2", {"start": v(53.11, -91.21) * mm, "end": v(48.49, -91.21) * mm});
            skLineSegment(sketch, "E3.12.1.3", {"start": v(48.49, -91.21) * mm, "end": v(48.49, -86.59) * mm});
            skLineSegment(sketch, "E3.12.2.0", {"start": v(53.11, -73.89) * mm, "end": v(48.49, -73.89) * mm});
            skLineSegment(sketch, "E3.12.2.1", {"start": v(53.11, -78.51) * mm, "end": v(53.11, -73.89) * mm});
            skLineSegment(sketch, "E3.12.2.2", {"start": v(53.11, -78.51) * mm, "end": v(48.49, -78.51) * mm});
            skLineSegment(sketch, "E3.12.2.3", {"start": v(48.49, -78.51) * mm, "end": v(48.49, -73.89) * mm});
            skLineSegment(sketch, "E3.12.3.0", {"start": v(53.11, -61.19) * mm, "end": v(48.49, -61.19) * mm});
            skLineSegment(sketch, "E3.12.3.1", {"start": v(53.11, -65.81) * mm, "end": v(53.11, -61.19) * mm});
            skLineSegment(sketch, "E3.12.3.2", {"start": v(53.11, -65.81) * mm, "end": v(48.49, -65.81) * mm});
            skLineSegment(sketch, "E3.12.3.3", {"start": v(48.49, -65.81) * mm, "end": v(48.49, -61.19) * mm});
            skLineSegment(sketch, "E3.12.4.0", {"start": v(53.11, -48.49) * mm, "end": v(48.49, -48.49) * mm});
            skLineSegment(sketch, "E3.12.4.1", {"start": v(53.11, -53.11) * mm, "end": v(53.11, -48.49) * mm});
            skLineSegment(sketch, "E3.12.4.2", {"start": v(53.11, -53.11) * mm, "end": v(48.49, -53.11) * mm});
            skLineSegment(sketch, "E3.12.4.3", {"start": v(48.49, -53.11) * mm, "end": v(48.49, -48.49) * mm});
            skLineSegment(sketch, "E3.12.5.0", {"start": v(53.11, -35.79) * mm, "end": v(48.49, -35.79) * mm});
            skLineSegment(sketch, "E3.12.5.1", {"start": v(53.11, -40.41) * mm, "end": v(53.11, -35.79) * mm});
            skLineSegment(sketch, "E3.12.5.2", {"start": v(53.11, -40.41) * mm, "end": v(48.49, -40.41) * mm});
            skLineSegment(sketch, "E3.12.5.3", {"start": v(48.49, -40.41) * mm, "end": v(48.49, -35.79) * mm});
            skLineSegment(sketch, "E3.12.6.0", {"start": v(53.11, -23.09) * mm, "end": v(48.49, -23.09) * mm});
            skLineSegment(sketch, "E3.12.6.1", {"start": v(53.11, -27.71) * mm, "end": v(53.11, -23.09) * mm});
            skLineSegment(sketch, "E3.12.6.2", {"start": v(53.11, -27.71) * mm, "end": v(48.49, -27.71) * mm});
            skLineSegment(sketch, "E3.12.6.3", {"start": v(48.49, -27.71) * mm, "end": v(48.49, -23.09) * mm});
            skLineSegment(sketch, "E3.12.7.0", {"start": v(53.11, -10.39) * mm, "end": v(48.49, -10.39) * mm});
            skLineSegment(sketch, "E3.12.7.1", {"start": v(53.11, -15.01) * mm, "end": v(53.11, -10.39) * mm});
            skLineSegment(sketch, "E3.12.7.2", {"start": v(53.11, -15.01) * mm, "end": v(48.49, -15.01) * mm});
            skLineSegment(sketch, "E3.12.7.3", {"start": v(48.49, -15.01) * mm, "end": v(48.49, -10.39) * mm});
            skLineSegment(sketch, "E3.12.8.0", {"start": v(53.11, 2.31) * mm, "end": v(48.49, 2.31) * mm});
            skLineSegment(sketch, "E3.12.8.1", {"start": v(53.11, -2.31) * mm, "end": v(53.11, 2.31) * mm});
            skLineSegment(sketch, "E3.12.8.2", {"start": v(53.11, -2.31) * mm, "end": v(48.49, -2.31) * mm});
            skLineSegment(sketch, "E3.12.8.3", {"start": v(48.49, -2.31) * mm, "end": v(48.49, 2.31) * mm});
            skLineSegment(sketch, "E3.12.9.0", {"start": v(53.11, 15.01) * mm, "end": v(48.49, 15.01) * mm});
            skLineSegment(sketch, "E3.12.9.1", {"start": v(53.11, 10.39) * mm, "end": v(53.11, 15.01) * mm});
            skLineSegment(sketch, "E3.12.9.2", {"start": v(53.11, 10.39) * mm, "end": v(48.49, 10.39) * mm});
            skLineSegment(sketch, "E3.12.9.3", {"start": v(48.49, 10.39) * mm, "end": v(48.49, 15.01) * mm});
            skLineSegment(sketch, "E3.12.10.0", {"start": v(53.11, 27.71) * mm, "end": v(48.49, 27.71) * mm});
            skLineSegment(sketch, "E3.12.10.1", {"start": v(53.11, 23.09) * mm, "end": v(53.11, 27.71) * mm});
            skLineSegment(sketch, "E3.12.10.2", {"start": v(53.11, 23.09) * mm, "end": v(48.49, 23.09) * mm});
            skLineSegment(sketch, "E3.12.10.3", {"start": v(48.49, 23.09) * mm, "end": v(48.49, 27.71) * mm});
            skLineSegment(sketch, "E3.12.11.0", {"start": v(53.11, 40.41) * mm, "end": v(48.49, 40.41) * mm});
            skLineSegment(sketch, "E3.12.11.1", {"start": v(53.11, 35.79) * mm, "end": v(53.11, 40.41) * mm});
            skLineSegment(sketch, "E3.12.11.2", {"start": v(53.11, 35.79) * mm, "end": v(48.49, 35.79) * mm});
            skLineSegment(sketch, "E3.12.11.3", {"start": v(48.49, 35.79) * mm, "end": v(48.49, 40.41) * mm});
            skLineSegment(sketch, "E3.12.12.0", {"start": v(53.11, 53.11) * mm, "end": v(48.49, 53.11) * mm});
            skLineSegment(sketch, "E3.12.12.1", {"start": v(53.11, 48.49) * mm, "end": v(53.11, 53.11) * mm});
            skLineSegment(sketch, "E3.12.12.2", {"start": v(53.11, 48.49) * mm, "end": v(48.49, 48.49) * mm});
            skLineSegment(sketch, "E3.12.12.3", {"start": v(48.49, 48.49) * mm, "end": v(48.49, 53.11) * mm});
            skLineSegment(sketch, "E3.12.13.0", {"start": v(53.11, 65.81) * mm, "end": v(48.49, 65.81) * mm});
            skLineSegment(sketch, "E3.12.13.1", {"start": v(53.11, 61.19) * mm, "end": v(53.11, 65.81) * mm});
            skLineSegment(sketch, "E3.12.13.2", {"start": v(53.11, 61.19) * mm, "end": v(48.49, 61.19) * mm});
            skLineSegment(sketch, "E3.12.13.3", {"start": v(48.49, 61.19) * mm, "end": v(48.49, 65.81) * mm});
            skLineSegment(sketch, "E3.12.14.0", {"start": v(53.11, 78.51) * mm, "end": v(48.49, 78.51) * mm});
            skLineSegment(sketch, "E3.12.14.1", {"start": v(53.11, 73.89) * mm, "end": v(53.11, 78.51) * mm});
            skLineSegment(sketch, "E3.12.14.2", {"start": v(53.11, 73.89) * mm, "end": v(48.49, 73.89) * mm});
            skLineSegment(sketch, "E3.12.14.3", {"start": v(48.49, 73.89) * mm, "end": v(48.49, 78.51) * mm});
            skLineSegment(sketch, "E3.12.15.0", {"start": v(53.11, 91.21) * mm, "end": v(48.49, 91.21) * mm});
            skLineSegment(sketch, "E3.12.15.1", {"start": v(53.11, 86.59) * mm, "end": v(53.11, 91.21) * mm});
            skLineSegment(sketch, "E3.12.15.2", {"start": v(53.11, 86.59) * mm, "end": v(48.49, 86.59) * mm});
            skLineSegment(sketch, "E3.12.15.3", {"start": v(48.49, 86.59) * mm, "end": v(48.49, 91.21) * mm});
            skLineSegment(sketch, "E3.12.16.0", {"start": v(53.11, 103.91) * mm, "end": v(48.49, 103.91) * mm});
            skLineSegment(sketch, "E3.12.16.1", {"start": v(53.11, 99.29) * mm, "end": v(53.11, 103.91) * mm});
            skLineSegment(sketch, "E3.12.16.2", {"start": v(53.11, 99.29) * mm, "end": v(48.49, 99.29) * mm});
            skLineSegment(sketch, "E3.12.16.3", {"start": v(48.49, 99.29) * mm, "end": v(48.49, 103.91) * mm});
            skLineSegment(sketch, "E3.13.0.0", {"start": v(65.81, -99.29) * mm, "end": v(61.19, -99.29) * mm});
            skLineSegment(sketch, "E3.13.0.1", {"start": v(65.81, -103.91) * mm, "end": v(65.81, -99.29) * mm});
            skLineSegment(sketch, "E3.13.0.2", {"start": v(65.81, -103.91) * mm, "end": v(61.19, -103.91) * mm});
            skLineSegment(sketch, "E3.13.0.3", {"start": v(61.19, -103.91) * mm, "end": v(61.19, -99.29) * mm});
            skLineSegment(sketch, "E3.13.1.0", {"start": v(65.81, -86.59) * mm, "end": v(61.19, -86.59) * mm});
            skLineSegment(sketch, "E3.13.1.1", {"start": v(65.81, -91.21) * mm, "end": v(65.81, -86.59) * mm});
            skLineSegment(sketch, "E3.13.1.2", {"start": v(65.81, -91.21) * mm, "end": v(61.19, -91.21) * mm});
            skLineSegment(sketch, "E3.13.1.3", {"start": v(61.19, -91.21) * mm, "end": v(61.19, -86.59) * mm});
            skLineSegment(sketch, "E3.13.2.0", {"start": v(65.81, -73.89) * mm, "end": v(61.19, -73.89) * mm});
            skLineSegment(sketch, "E3.13.2.1", {"start": v(65.81, -78.51) * mm, "end": v(65.81, -73.89) * mm});
            skLineSegment(sketch, "E3.13.2.2", {"start": v(65.81, -78.51) * mm, "end": v(61.19, -78.51) * mm});
            skLineSegment(sketch, "E3.13.2.3", {"start": v(61.19, -78.51) * mm, "end": v(61.19, -73.89) * mm});
            skLineSegment(sketch, "E3.13.3.0", {"start": v(65.81, -61.19) * mm, "end": v(61.19, -61.19) * mm});
            skLineSegment(sketch, "E3.13.3.1", {"start": v(65.81, -65.81) * mm, "end": v(65.81, -61.19) * mm});
            skLineSegment(sketch, "E3.13.3.2", {"start": v(65.81, -65.81) * mm, "end": v(61.19, -65.81) * mm});
            skLineSegment(sketch, "E3.13.3.3", {"start": v(61.19, -65.81) * mm, "end": v(61.19, -61.19) * mm});
            skLineSegment(sketch, "E3.13.4.0", {"start": v(65.81, -48.49) * mm, "end": v(61.19, -48.49) * mm});
            skLineSegment(sketch, "E3.13.4.1", {"start": v(65.81, -53.11) * mm, "end": v(65.81, -48.49) * mm});
            skLineSegment(sketch, "E3.13.4.2", {"start": v(65.81, -53.11) * mm, "end": v(61.19, -53.11) * mm});
            skLineSegment(sketch, "E3.13.4.3", {"start": v(61.19, -53.11) * mm, "end": v(61.19, -48.49) * mm});
            skLineSegment(sketch, "E3.13.5.0", {"start": v(65.81, -35.79) * mm, "end": v(61.19, -35.79) * mm});
            skLineSegment(sketch, "E3.13.5.1", {"start": v(65.81, -40.41) * mm, "end": v(65.81, -35.79) * mm});
            skLineSegment(sketch, "E3.13.5.2", {"start": v(65.81, -40.41) * mm, "end": v(61.19, -40.41) * mm});
            skLineSegment(sketch, "E3.13.5.3", {"start": v(61.19, -40.41) * mm, "end": v(61.19, -35.79) * mm});
            skLineSegment(sketch, "E3.13.6.0", {"start": v(65.81, -23.09) * mm, "end": v(61.19, -23.09) * mm});
            skLineSegment(sketch, "E3.13.6.1", {"start": v(65.81, -27.71) * mm, "end": v(65.81, -23.09) * mm});
            skLineSegment(sketch, "E3.13.6.2", {"start": v(65.81, -27.71) * mm, "end": v(61.19, -27.71) * mm});
            skLineSegment(sketch, "E3.13.6.3", {"start": v(61.19, -27.71) * mm, "end": v(61.19, -23.09) * mm});
            skLineSegment(sketch, "E3.13.7.0", {"start": v(65.81, -10.39) * mm, "end": v(61.19, -10.39) * mm});
            skLineSegment(sketch, "E3.13.7.1", {"start": v(65.81, -15.01) * mm, "end": v(65.81, -10.39) * mm});
            skLineSegment(sketch, "E3.13.7.2", {"start": v(65.81, -15.01) * mm, "end": v(61.19, -15.01) * mm});
            skLineSegment(sketch, "E3.13.7.3", {"start": v(61.19, -15.01) * mm, "end": v(61.19, -10.39) * mm});
            skLineSegment(sketch, "E3.13.8.0", {"start": v(65.81, 2.31) * mm, "end": v(61.19, 2.31) * mm});
            skLineSegment(sketch, "E3.13.8.1", {"start": v(65.81, -2.31) * mm, "end": v(65.81, 2.31) * mm});
            skLineSegment(sketch, "E3.13.8.2", {"start": v(65.81, -2.31) * mm, "end": v(61.19, -2.31) * mm});
            skLineSegment(sketch, "E3.13.8.3", {"start": v(61.19, -2.31) * mm, "end": v(61.19, 2.31) * mm});
            skLineSegment(sketch, "E3.13.9.0", {"start": v(65.81, 15.01) * mm, "end": v(61.19, 15.01) * mm});
            skLineSegment(sketch, "E3.13.9.1", {"start": v(65.81, 10.39) * mm, "end": v(65.81, 15.01) * mm});
            skLineSegment(sketch, "E3.13.9.2", {"start": v(65.81, 10.39) * mm, "end": v(61.19, 10.39) * mm});
            skLineSegment(sketch, "E3.13.9.3", {"start": v(61.19, 10.39) * mm, "end": v(61.19, 15.01) * mm});
            skLineSegment(sketch, "E3.13.10.0", {"start": v(65.81, 27.71) * mm, "end": v(61.19, 27.71) * mm});
            skLineSegment(sketch, "E3.13.10.1", {"start": v(65.81, 23.09) * mm, "end": v(65.81, 27.71) * mm});
            skLineSegment(sketch, "E3.13.10.2", {"start": v(65.81, 23.09) * mm, "end": v(61.19, 23.09) * mm});
            skLineSegment(sketch, "E3.13.10.3", {"start": v(61.19, 23.09) * mm, "end": v(61.19, 27.71) * mm});
            skLineSegment(sketch, "E3.13.11.0", {"start": v(65.81, 40.41) * mm, "end": v(61.19, 40.41) * mm});
            skLineSegment(sketch, "E3.13.11.1", {"start": v(65.81, 35.79) * mm, "end": v(65.81, 40.41) * mm});
            skLineSegment(sketch, "E3.13.11.2", {"start": v(65.81, 35.79) * mm, "end": v(61.19, 35.79) * mm});
            skLineSegment(sketch, "E3.13.11.3", {"start": v(61.19, 35.79) * mm, "end": v(61.19, 40.41) * mm});
            skLineSegment(sketch, "E3.13.12.0", {"start": v(65.81, 53.11) * mm, "end": v(61.19, 53.11) * mm});
            skLineSegment(sketch, "E3.13.12.1", {"start": v(65.81, 48.49) * mm, "end": v(65.81, 53.11) * mm});
            skLineSegment(sketch, "E3.13.12.2", {"start": v(65.81, 48.49) * mm, "end": v(61.19, 48.49) * mm});
            skLineSegment(sketch, "E3.13.12.3", {"start": v(61.19, 48.49) * mm, "end": v(61.19, 53.11) * mm});
            skLineSegment(sketch, "E3.13.13.0", {"start": v(65.81, 65.81) * mm, "end": v(61.19, 65.81) * mm});
            skLineSegment(sketch, "E3.13.13.1", {"start": v(65.81, 61.19) * mm, "end": v(65.81, 65.81) * mm});
            skLineSegment(sketch, "E3.13.13.2", {"start": v(65.81, 61.19) * mm, "end": v(61.19, 61.19) * mm});
            skLineSegment(sketch, "E3.13.13.3", {"start": v(61.19, 61.19) * mm, "end": v(61.19, 65.81) * mm});
            skLineSegment(sketch, "E3.13.14.0", {"start": v(65.81, 78.51) * mm, "end": v(61.19, 78.51) * mm});
            skLineSegment(sketch, "E3.13.14.1", {"start": v(65.81, 73.89) * mm, "end": v(65.81, 78.51) * mm});
            skLineSegment(sketch, "E3.13.14.2", {"start": v(65.81, 73.89) * mm, "end": v(61.19, 73.89) * mm});
            skLineSegment(sketch, "E3.13.14.3", {"start": v(61.19, 73.89) * mm, "end": v(61.19, 78.51) * mm});
            skLineSegment(sketch, "E3.13.15.0", {"start": v(65.81, 91.21) * mm, "end": v(61.19, 91.21) * mm});
            skLineSegment(sketch, "E3.13.15.1", {"start": v(65.81, 86.59) * mm, "end": v(65.81, 91.21) * mm});
            skLineSegment(sketch, "E3.13.15.2", {"start": v(65.81, 86.59) * mm, "end": v(61.19, 86.59) * mm});
            skLineSegment(sketch, "E3.13.15.3", {"start": v(61.19, 86.59) * mm, "end": v(61.19, 91.21) * mm});
            skLineSegment(sketch, "E3.13.16.0", {"start": v(65.81, 103.91) * mm, "end": v(61.19, 103.91) * mm});
            skLineSegment(sketch, "E3.13.16.1", {"start": v(65.81, 99.29) * mm, "end": v(65.81, 103.91) * mm});
            skLineSegment(sketch, "E3.13.16.2", {"start": v(65.81, 99.29) * mm, "end": v(61.19, 99.29) * mm});
            skLineSegment(sketch, "E3.13.16.3", {"start": v(61.19, 99.29) * mm, "end": v(61.19, 103.91) * mm});
            skLineSegment(sketch, "E3.14.0.0", {"start": v(78.51, -99.29) * mm, "end": v(73.89, -99.29) * mm});
            skLineSegment(sketch, "E3.14.0.1", {"start": v(78.51, -103.91) * mm, "end": v(78.51, -99.29) * mm});
            skLineSegment(sketch, "E3.14.0.2", {"start": v(78.51, -103.91) * mm, "end": v(73.89, -103.91) * mm});
            skLineSegment(sketch, "E3.14.0.3", {"start": v(73.89, -103.91) * mm, "end": v(73.89, -99.29) * mm});
            skLineSegment(sketch, "E3.14.1.0", {"start": v(78.51, -86.59) * mm, "end": v(73.89, -86.59) * mm});
            skLineSegment(sketch, "E3.14.1.1", {"start": v(78.51, -91.21) * mm, "end": v(78.51, -86.59) * mm});
            skLineSegment(sketch, "E3.14.1.2", {"start": v(78.51, -91.21) * mm, "end": v(73.89, -91.21) * mm});
            skLineSegment(sketch, "E3.14.1.3", {"start": v(73.89, -91.21) * mm, "end": v(73.89, -86.59) * mm});
            skLineSegment(sketch, "E3.14.2.0", {"start": v(78.51, -73.89) * mm, "end": v(73.89, -73.89) * mm});
            skLineSegment(sketch, "E3.14.2.1", {"start": v(78.51, -78.51) * mm, "end": v(78.51, -73.89) * mm});
            skLineSegment(sketch, "E3.14.2.2", {"start": v(78.51, -78.51) * mm, "end": v(73.89, -78.51) * mm});
            skLineSegment(sketch, "E3.14.2.3", {"start": v(73.89, -78.51) * mm, "end": v(73.89, -73.89) * mm});
            skLineSegment(sketch, "E3.14.3.0", {"start": v(78.51, -61.19) * mm, "end": v(73.89, -61.19) * mm});
            skLineSegment(sketch, "E3.14.3.1", {"start": v(78.51, -65.81) * mm, "end": v(78.51, -61.19) * mm});
            skLineSegment(sketch, "E3.14.3.2", {"start": v(78.51, -65.81) * mm, "end": v(73.89, -65.81) * mm});
            skLineSegment(sketch, "E3.14.3.3", {"start": v(73.89, -65.81) * mm, "end": v(73.89, -61.19) * mm});
            skLineSegment(sketch, "E3.14.4.0", {"start": v(78.51, -48.49) * mm, "end": v(73.89, -48.49) * mm});
            skLineSegment(sketch, "E3.14.4.1", {"start": v(78.51, -53.11) * mm, "end": v(78.51, -48.49) * mm});
            skLineSegment(sketch, "E3.14.4.2", {"start": v(78.51, -53.11) * mm, "end": v(73.89, -53.11) * mm});
            skLineSegment(sketch, "E3.14.4.3", {"start": v(73.89, -53.11) * mm, "end": v(73.89, -48.49) * mm});
            skLineSegment(sketch, "E3.14.5.0", {"start": v(78.51, -35.79) * mm, "end": v(73.89, -35.79) * mm});
            skLineSegment(sketch, "E3.14.5.1", {"start": v(78.51, -40.41) * mm, "end": v(78.51, -35.79) * mm});
            skLineSegment(sketch, "E3.14.5.2", {"start": v(78.51, -40.41) * mm, "end": v(73.89, -40.41) * mm});
            skLineSegment(sketch, "E3.14.5.3", {"start": v(73.89, -40.41) * mm, "end": v(73.89, -35.79) * mm});
            skLineSegment(sketch, "E3.14.6.0", {"start": v(78.51, -23.09) * mm, "end": v(73.89, -23.09) * mm});
            skLineSegment(sketch, "E3.14.6.1", {"start": v(78.51, -27.71) * mm, "end": v(78.51, -23.09) * mm});
            skLineSegment(sketch, "E3.14.6.2", {"start": v(78.51, -27.71) * mm, "end": v(73.89, -27.71) * mm});
            skLineSegment(sketch, "E3.14.6.3", {"start": v(73.89, -27.71) * mm, "end": v(73.89, -23.09) * mm});
            skLineSegment(sketch, "E3.14.7.0", {"start": v(78.51, -10.39) * mm, "end": v(73.89, -10.39) * mm});
            skLineSegment(sketch, "E3.14.7.1", {"start": v(78.51, -15.01) * mm, "end": v(78.51, -10.39) * mm});
            skLineSegment(sketch, "E3.14.7.2", {"start": v(78.51, -15.01) * mm, "end": v(73.89, -15.01) * mm});
            skLineSegment(sketch, "E3.14.7.3", {"start": v(73.89, -15.01) * mm, "end": v(73.89, -10.39) * mm});
            skLineSegment(sketch, "E3.14.8.0", {"start": v(78.51, 2.31) * mm, "end": v(73.89, 2.31) * mm});
            skLineSegment(sketch, "E3.14.8.1", {"start": v(78.51, -2.31) * mm, "end": v(78.51, 2.31) * mm});
            skLineSegment(sketch, "E3.14.8.2", {"start": v(78.51, -2.31) * mm, "end": v(73.89, -2.31) * mm});
            skLineSegment(sketch, "E3.14.8.3", {"start": v(73.89, -2.31) * mm, "end": v(73.89, 2.31) * mm});
            skLineSegment(sketch, "E3.14.9.0", {"start": v(78.51, 15.01) * mm, "end": v(73.89, 15.01) * mm});
            skLineSegment(sketch, "E3.14.9.1", {"start": v(78.51, 10.39) * mm, "end": v(78.51, 15.01) * mm});
            skLineSegment(sketch, "E3.14.9.2", {"start": v(78.51, 10.39) * mm, "end": v(73.89, 10.39) * mm});
            skLineSegment(sketch, "E3.14.9.3", {"start": v(73.89, 10.39) * mm, "end": v(73.89, 15.01) * mm});
            skLineSegment(sketch, "E3.14.10.0", {"start": v(78.51, 27.71) * mm, "end": v(73.89, 27.71) * mm});
            skLineSegment(sketch, "E3.14.10.1", {"start": v(78.51, 23.09) * mm, "end": v(78.51, 27.71) * mm});
            skLineSegment(sketch, "E3.14.10.2", {"start": v(78.51, 23.09) * mm, "end": v(73.89, 23.09) * mm});
            skLineSegment(sketch, "E3.14.10.3", {"start": v(73.89, 23.09) * mm, "end": v(73.89, 27.71) * mm});
            skLineSegment(sketch, "E3.14.11.0", {"start": v(78.51, 40.41) * mm, "end": v(73.89, 40.41) * mm});
            skLineSegment(sketch, "E3.14.11.1", {"start": v(78.51, 35.79) * mm, "end": v(78.51, 40.41) * mm});
            skLineSegment(sketch, "E3.14.11.2", {"start": v(78.51, 35.79) * mm, "end": v(73.89, 35.79) * mm});
            skLineSegment(sketch, "E3.14.11.3", {"start": v(73.89, 35.79) * mm, "end": v(73.89, 40.41) * mm});
            skLineSegment(sketch, "E3.14.12.0", {"start": v(78.51, 53.11) * mm, "end": v(73.89, 53.11) * mm});
            skLineSegment(sketch, "E3.14.12.1", {"start": v(78.51, 48.49) * mm, "end": v(78.51, 53.11) * mm});
            skLineSegment(sketch, "E3.14.12.2", {"start": v(78.51, 48.49) * mm, "end": v(73.89, 48.49) * mm});
            skLineSegment(sketch, "E3.14.12.3", {"start": v(73.89, 48.49) * mm, "end": v(73.89, 53.11) * mm});
            skLineSegment(sketch, "E3.14.13.0", {"start": v(78.51, 65.81) * mm, "end": v(73.89, 65.81) * mm});
            skLineSegment(sketch, "E3.14.13.1", {"start": v(78.51, 61.19) * mm, "end": v(78.51, 65.81) * mm});
            skLineSegment(sketch, "E3.14.13.2", {"start": v(78.51, 61.19) * mm, "end": v(73.89, 61.19) * mm});
            skLineSegment(sketch, "E3.14.13.3", {"start": v(73.89, 61.19) * mm, "end": v(73.89, 65.81) * mm});
            skLineSegment(sketch, "E3.14.14.0", {"start": v(78.51, 78.51) * mm, "end": v(73.89, 78.51) * mm});
            skLineSegment(sketch, "E3.14.14.1", {"start": v(78.51, 73.89) * mm, "end": v(78.51, 78.51) * mm});
            skLineSegment(sketch, "E3.14.14.2", {"start": v(78.51, 73.89) * mm, "end": v(73.89, 73.89) * mm});
            skLineSegment(sketch, "E3.14.14.3", {"start": v(73.89, 73.89) * mm, "end": v(73.89, 78.51) * mm});
            skLineSegment(sketch, "E3.14.15.0", {"start": v(78.51, 91.21) * mm, "end": v(73.89, 91.21) * mm});
            skLineSegment(sketch, "E3.14.15.1", {"start": v(78.51, 86.59) * mm, "end": v(78.51, 91.21) * mm});
            skLineSegment(sketch, "E3.14.15.2", {"start": v(78.51, 86.59) * mm, "end": v(73.89, 86.59) * mm});
            skLineSegment(sketch, "E3.14.15.3", {"start": v(73.89, 86.59) * mm, "end": v(73.89, 91.21) * mm});
            skLineSegment(sketch, "E3.14.16.0", {"start": v(78.51, 103.91) * mm, "end": v(73.89, 103.91) * mm});
            skLineSegment(sketch, "E3.14.16.1", {"start": v(78.51, 99.29) * mm, "end": v(78.51, 103.91) * mm});
            skLineSegment(sketch, "E3.14.16.2", {"start": v(78.51, 99.29) * mm, "end": v(73.89, 99.29) * mm});
            skLineSegment(sketch, "E3.14.16.3", {"start": v(73.89, 99.29) * mm, "end": v(73.89, 103.91) * mm});
            skLineSegment(sketch, "E3.15.0.0", {"start": v(91.21, -99.29) * mm, "end": v(86.59, -99.29) * mm});
            skLineSegment(sketch, "E3.15.0.1", {"start": v(91.21, -103.91) * mm, "end": v(91.21, -99.29) * mm});
            skLineSegment(sketch, "E3.15.0.2", {"start": v(91.21, -103.91) * mm, "end": v(86.59, -103.91) * mm});
            skLineSegment(sketch, "E3.15.0.3", {"start": v(86.59, -103.91) * mm, "end": v(86.59, -99.29) * mm});
            skLineSegment(sketch, "E3.15.1.0", {"start": v(91.21, -86.59) * mm, "end": v(86.59, -86.59) * mm});
            skLineSegment(sketch, "E3.15.1.1", {"start": v(91.21, -91.21) * mm, "end": v(91.21, -86.59) * mm});
            skLineSegment(sketch, "E3.15.1.2", {"start": v(91.21, -91.21) * mm, "end": v(86.59, -91.21) * mm});
            skLineSegment(sketch, "E3.15.1.3", {"start": v(86.59, -91.21) * mm, "end": v(86.59, -86.59) * mm});
            skLineSegment(sketch, "E3.15.2.0", {"start": v(91.21, -73.89) * mm, "end": v(86.59, -73.89) * mm});
            skLineSegment(sketch, "E3.15.2.1", {"start": v(91.21, -78.51) * mm, "end": v(91.21, -73.89) * mm});
            skLineSegment(sketch, "E3.15.2.2", {"start": v(91.21, -78.51) * mm, "end": v(86.59, -78.51) * mm});
            skLineSegment(sketch, "E3.15.2.3", {"start": v(86.59, -78.51) * mm, "end": v(86.59, -73.89) * mm});
            skLineSegment(sketch, "E3.15.3.0", {"start": v(91.21, -61.19) * mm, "end": v(86.59, -61.19) * mm});
            skLineSegment(sketch, "E3.15.3.1", {"start": v(91.21, -65.81) * mm, "end": v(91.21, -61.19) * mm});
            skLineSegment(sketch, "E3.15.3.2", {"start": v(91.21, -65.81) * mm, "end": v(86.59, -65.81) * mm});
            skLineSegment(sketch, "E3.15.3.3", {"start": v(86.59, -65.81) * mm, "end": v(86.59, -61.19) * mm});
            skLineSegment(sketch, "E3.15.4.0", {"start": v(91.21, -48.49) * mm, "end": v(86.59, -48.49) * mm});
            skLineSegment(sketch, "E3.15.4.1", {"start": v(91.21, -53.11) * mm, "end": v(91.21, -48.49) * mm});
            skLineSegment(sketch, "E3.15.4.2", {"start": v(91.21, -53.11) * mm, "end": v(86.59, -53.11) * mm});
            skLineSegment(sketch, "E3.15.4.3", {"start": v(86.59, -53.11) * mm, "end": v(86.59, -48.49) * mm});
            skLineSegment(sketch, "E3.15.5.0", {"start": v(91.21, -35.79) * mm, "end": v(86.59, -35.79) * mm});
            skLineSegment(sketch, "E3.15.5.1", {"start": v(91.21, -40.41) * mm, "end": v(91.21, -35.79) * mm});
            skLineSegment(sketch, "E3.15.5.2", {"start": v(91.21, -40.41) * mm, "end": v(86.59, -40.41) * mm});
            skLineSegment(sketch, "E3.15.5.3", {"start": v(86.59, -40.41) * mm, "end": v(86.59, -35.79) * mm});
            skLineSegment(sketch, "E3.15.6.0", {"start": v(91.21, -23.09) * mm, "end": v(86.59, -23.09) * mm});
            skLineSegment(sketch, "E3.15.6.1", {"start": v(91.21, -27.71) * mm, "end": v(91.21, -23.09) * mm});
            skLineSegment(sketch, "E3.15.6.2", {"start": v(91.21, -27.71) * mm, "end": v(86.59, -27.71) * mm});
            skLineSegment(sketch, "E3.15.6.3", {"start": v(86.59, -27.71) * mm, "end": v(86.59, -23.09) * mm});
            skLineSegment(sketch, "E3.15.7.0", {"start": v(91.21, -10.39) * mm, "end": v(86.59, -10.39) * mm});
            skLineSegment(sketch, "E3.15.7.1", {"start": v(91.21, -15.01) * mm, "end": v(91.21, -10.39) * mm});
            skLineSegment(sketch, "E3.15.7.2", {"start": v(91.21, -15.01) * mm, "end": v(86.59, -15.01) * mm});
            skLineSegment(sketch, "E3.15.7.3", {"start": v(86.59, -15.01) * mm, "end": v(86.59, -10.39) * mm});
            skLineSegment(sketch, "E3.15.8.0", {"start": v(91.21, 2.31) * mm, "end": v(86.59, 2.31) * mm});
            skLineSegment(sketch, "E3.15.8.1", {"start": v(91.21, -2.31) * mm, "end": v(91.21, 2.31) * mm});
            skLineSegment(sketch, "E3.15.8.2", {"start": v(91.21, -2.31) * mm, "end": v(86.59, -2.31) * mm});
            skLineSegment(sketch, "E3.15.8.3", {"start": v(86.59, -2.31) * mm, "end": v(86.59, 2.31) * mm});
            skLineSegment(sketch, "E3.15.9.0", {"start": v(91.21, 15.01) * mm, "end": v(86.59, 15.01) * mm});
            skLineSegment(sketch, "E3.15.9.1", {"start": v(91.21, 10.39) * mm, "end": v(91.21, 15.01) * mm});
            skLineSegment(sketch, "E3.15.9.2", {"start": v(91.21, 10.39) * mm, "end": v(86.59, 10.39) * mm});
            skLineSegment(sketch, "E3.15.9.3", {"start": v(86.59, 10.39) * mm, "end": v(86.59, 15.01) * mm});
            skLineSegment(sketch, "E3.15.10.0", {"start": v(91.21, 27.71) * mm, "end": v(86.59, 27.71) * mm});
            skLineSegment(sketch, "E3.15.10.1", {"start": v(91.21, 23.09) * mm, "end": v(91.21, 27.71) * mm});
            skLineSegment(sketch, "E3.15.10.2", {"start": v(91.21, 23.09) * mm, "end": v(86.59, 23.09) * mm});
            skLineSegment(sketch, "E3.15.10.3", {"start": v(86.59, 23.09) * mm, "end": v(86.59, 27.71) * mm});
            skLineSegment(sketch, "E3.15.11.0", {"start": v(91.21, 40.41) * mm, "end": v(86.59, 40.41) * mm});
            skLineSegment(sketch, "E3.15.11.1", {"start": v(91.21, 35.79) * mm, "end": v(91.21, 40.41) * mm});
            skLineSegment(sketch, "E3.15.11.2", {"start": v(91.21, 35.79) * mm, "end": v(86.59, 35.79) * mm});
            skLineSegment(sketch, "E3.15.11.3", {"start": v(86.59, 35.79) * mm, "end": v(86.59, 40.41) * mm});
            skLineSegment(sketch, "E3.15.12.0", {"start": v(91.21, 53.11) * mm, "end": v(86.59, 53.11) * mm});
            skLineSegment(sketch, "E3.15.12.1", {"start": v(91.21, 48.49) * mm, "end": v(91.21, 53.11) * mm});
            skLineSegment(sketch, "E3.15.12.2", {"start": v(91.21, 48.49) * mm, "end": v(86.59, 48.49) * mm});
            skLineSegment(sketch, "E3.15.12.3", {"start": v(86.59, 48.49) * mm, "end": v(86.59, 53.11) * mm});
            skLineSegment(sketch, "E3.15.13.0", {"start": v(91.21, 65.81) * mm, "end": v(86.59, 65.81) * mm});
            skLineSegment(sketch, "E3.15.13.1", {"start": v(91.21, 61.19) * mm, "end": v(91.21, 65.81) * mm});
            skLineSegment(sketch, "E3.15.13.2", {"start": v(91.21, 61.19) * mm, "end": v(86.59, 61.19) * mm});
            skLineSegment(sketch, "E3.15.13.3", {"start": v(86.59, 61.19) * mm, "end": v(86.59, 65.81) * mm});
            skLineSegment(sketch, "E3.15.14.0", {"start": v(91.21, 78.51) * mm, "end": v(86.59, 78.51) * mm});
            skLineSegment(sketch, "E3.15.14.1", {"start": v(91.21, 73.89) * mm, "end": v(91.21, 78.51) * mm});
            skLineSegment(sketch, "E3.15.14.2", {"start": v(91.21, 73.89) * mm, "end": v(86.59, 73.89) * mm});
            skLineSegment(sketch, "E3.15.14.3", {"start": v(86.59, 73.89) * mm, "end": v(86.59, 78.51) * mm});
            skLineSegment(sketch, "E3.15.15.0", {"start": v(91.21, 91.21) * mm, "end": v(86.59, 91.21) * mm});
            skLineSegment(sketch, "E3.15.15.1", {"start": v(91.21, 86.59) * mm, "end": v(91.21, 91.21) * mm});
            skLineSegment(sketch, "E3.15.15.2", {"start": v(91.21, 86.59) * mm, "end": v(86.59, 86.59) * mm});
            skLineSegment(sketch, "E3.15.15.3", {"start": v(86.59, 86.59) * mm, "end": v(86.59, 91.21) * mm});
            skLineSegment(sketch, "E3.15.16.0", {"start": v(91.21, 103.91) * mm, "end": v(86.59, 103.91) * mm});
            skLineSegment(sketch, "E3.15.16.1", {"start": v(91.21, 99.29) * mm, "end": v(91.21, 103.91) * mm});
            skLineSegment(sketch, "E3.15.16.2", {"start": v(91.21, 99.29) * mm, "end": v(86.59, 99.29) * mm});
            skLineSegment(sketch, "E3.15.16.3", {"start": v(86.59, 99.29) * mm, "end": v(86.59, 103.91) * mm});
            skLineSegment(sketch, "E3.16.0.0", {"start": v(103.91, -99.29) * mm, "end": v(99.29, -99.29) * mm});
            skLineSegment(sketch, "E3.16.0.1", {"start": v(103.91, -103.91) * mm, "end": v(103.91, -99.29) * mm});
            skLineSegment(sketch, "E3.16.0.2", {"start": v(103.91, -103.91) * mm, "end": v(99.29, -103.91) * mm});
            skLineSegment(sketch, "E3.16.0.3", {"start": v(99.29, -103.91) * mm, "end": v(99.29, -99.29) * mm});
            skLineSegment(sketch, "E3.16.1.0", {"start": v(103.91, -86.59) * mm, "end": v(99.29, -86.59) * mm});
            skLineSegment(sketch, "E3.16.1.1", {"start": v(103.91, -91.21) * mm, "end": v(103.91, -86.59) * mm});
            skLineSegment(sketch, "E3.16.1.2", {"start": v(103.91, -91.21) * mm, "end": v(99.29, -91.21) * mm});
            skLineSegment(sketch, "E3.16.1.3", {"start": v(99.29, -91.21) * mm, "end": v(99.29, -86.59) * mm});
            skLineSegment(sketch, "E3.16.2.0", {"start": v(103.91, -73.89) * mm, "end": v(99.29, -73.89) * mm});
            skLineSegment(sketch, "E3.16.2.1", {"start": v(103.91, -78.51) * mm, "end": v(103.91, -73.89) * mm});
            skLineSegment(sketch, "E3.16.2.2", {"start": v(103.91, -78.51) * mm, "end": v(99.29, -78.51) * mm});
            skLineSegment(sketch, "E3.16.2.3", {"start": v(99.29, -78.51) * mm, "end": v(99.29, -73.89) * mm});
            skLineSegment(sketch, "E3.16.3.0", {"start": v(103.91, -61.19) * mm, "end": v(99.29, -61.19) * mm});
            skLineSegment(sketch, "E3.16.3.1", {"start": v(103.91, -65.81) * mm, "end": v(103.91, -61.19) * mm});
            skLineSegment(sketch, "E3.16.3.2", {"start": v(103.91, -65.81) * mm, "end": v(99.29, -65.81) * mm});
            skLineSegment(sketch, "E3.16.3.3", {"start": v(99.29, -65.81) * mm, "end": v(99.29, -61.19) * mm});
            skLineSegment(sketch, "E3.16.4.0", {"start": v(103.91, -48.49) * mm, "end": v(99.29, -48.49) * mm});
            skLineSegment(sketch, "E3.16.4.1", {"start": v(103.91, -53.11) * mm, "end": v(103.91, -48.49) * mm});
            skLineSegment(sketch, "E3.16.4.2", {"start": v(103.91, -53.11) * mm, "end": v(99.29, -53.11) * mm});
            skLineSegment(sketch, "E3.16.4.3", {"start": v(99.29, -53.11) * mm, "end": v(99.29, -48.49) * mm});
            skLineSegment(sketch, "E3.16.5.0", {"start": v(103.91, -35.79) * mm, "end": v(99.29, -35.79) * mm});
            skLineSegment(sketch, "E3.16.5.1", {"start": v(103.91, -40.41) * mm, "end": v(103.91, -35.79) * mm});
            skLineSegment(sketch, "E3.16.5.2", {"start": v(103.91, -40.41) * mm, "end": v(99.29, -40.41) * mm});
            skLineSegment(sketch, "E3.16.5.3", {"start": v(99.29, -40.41) * mm, "end": v(99.29, -35.79) * mm});
            skLineSegment(sketch, "E3.16.6.0", {"start": v(103.91, -23.09) * mm, "end": v(99.29, -23.09) * mm});
            skLineSegment(sketch, "E3.16.6.1", {"start": v(103.91, -27.71) * mm, "end": v(103.91, -23.09) * mm});
            skLineSegment(sketch, "E3.16.6.2", {"start": v(103.91, -27.71) * mm, "end": v(99.29, -27.71) * mm});
            skLineSegment(sketch, "E3.16.6.3", {"start": v(99.29, -27.71) * mm, "end": v(99.29, -23.09) * mm});
            skLineSegment(sketch, "E3.16.7.0", {"start": v(103.91, -10.39) * mm, "end": v(99.29, -10.39) * mm});
            skLineSegment(sketch, "E3.16.7.1", {"start": v(103.91, -15.01) * mm, "end": v(103.91, -10.39) * mm});
            skLineSegment(sketch, "E3.16.7.2", {"start": v(103.91, -15.01) * mm, "end": v(99.29, -15.01) * mm});
            skLineSegment(sketch, "E3.16.7.3", {"start": v(99.29, -15.01) * mm, "end": v(99.29, -10.39) * mm});
            skLineSegment(sketch, "E3.16.8.0", {"start": v(103.91, 2.31) * mm, "end": v(99.29, 2.31) * mm});
            skLineSegment(sketch, "E3.16.8.1", {"start": v(103.91, -2.31) * mm, "end": v(103.91, 2.31) * mm});
            skLineSegment(sketch, "E3.16.8.2", {"start": v(103.91, -2.31) * mm, "end": v(99.29, -2.31) * mm});
            skLineSegment(sketch, "E3.16.8.3", {"start": v(99.29, -2.31) * mm, "end": v(99.29, 2.31) * mm});
            skLineSegment(sketch, "E3.16.9.0", {"start": v(103.91, 15.01) * mm, "end": v(99.29, 15.01) * mm});
            skLineSegment(sketch, "E3.16.9.1", {"start": v(103.91, 10.39) * mm, "end": v(103.91, 15.01) * mm});
            skLineSegment(sketch, "E3.16.9.2", {"start": v(103.91, 10.39) * mm, "end": v(99.29, 10.39) * mm});
            skLineSegment(sketch, "E3.16.9.3", {"start": v(99.29, 10.39) * mm, "end": v(99.29, 15.01) * mm});
            skLineSegment(sketch, "E3.16.10.0", {"start": v(103.91, 27.71) * mm, "end": v(99.29, 27.71) * mm});
            skLineSegment(sketch, "E3.16.10.1", {"start": v(103.91, 23.09) * mm, "end": v(103.91, 27.71) * mm});
            skLineSegment(sketch, "E3.16.10.2", {"start": v(103.91, 23.09) * mm, "end": v(99.29, 23.09) * mm});
            skLineSegment(sketch, "E3.16.10.3", {"start": v(99.29, 23.09) * mm, "end": v(99.29, 27.71) * mm});
            skLineSegment(sketch, "E3.16.11.0", {"start": v(103.91, 40.41) * mm, "end": v(99.29, 40.41) * mm});
            skLineSegment(sketch, "E3.16.11.1", {"start": v(103.91, 35.79) * mm, "end": v(103.91, 40.41) * mm});
            skLineSegment(sketch, "E3.16.11.2", {"start": v(103.91, 35.79) * mm, "end": v(99.29, 35.79) * mm});
            skLineSegment(sketch, "E3.16.11.3", {"start": v(99.29, 35.79) * mm, "end": v(99.29, 40.41) * mm});
            skLineSegment(sketch, "E3.16.12.0", {"start": v(103.91, 53.11) * mm, "end": v(99.29, 53.11) * mm});
            skLineSegment(sketch, "E3.16.12.1", {"start": v(103.91, 48.49) * mm, "end": v(103.91, 53.11) * mm});
            skLineSegment(sketch, "E3.16.12.2", {"start": v(103.91, 48.49) * mm, "end": v(99.29, 48.49) * mm});
            skLineSegment(sketch, "E3.16.12.3", {"start": v(99.29, 48.49) * mm, "end": v(99.29, 53.11) * mm});
            skLineSegment(sketch, "E3.16.13.0", {"start": v(103.91, 65.81) * mm, "end": v(99.29, 65.81) * mm});
            skLineSegment(sketch, "E3.16.13.1", {"start": v(103.91, 61.19) * mm, "end": v(103.91, 65.81) * mm});
            skLineSegment(sketch, "E3.16.13.2", {"start": v(103.91, 61.19) * mm, "end": v(99.29, 61.19) * mm});
            skLineSegment(sketch, "E3.16.13.3", {"start": v(99.29, 61.19) * mm, "end": v(99.29, 65.81) * mm});
            skLineSegment(sketch, "E3.16.14.0", {"start": v(103.91, 78.51) * mm, "end": v(99.29, 78.51) * mm});
            skLineSegment(sketch, "E3.16.14.1", {"start": v(103.91, 73.89) * mm, "end": v(103.91, 78.51) * mm});
            skLineSegment(sketch, "E3.16.14.2", {"start": v(103.91, 73.89) * mm, "end": v(99.29, 73.89) * mm});
            skLineSegment(sketch, "E3.16.14.3", {"start": v(99.29, 73.89) * mm, "end": v(99.29, 78.51) * mm});
            skLineSegment(sketch, "E3.16.15.0", {"start": v(103.91, 91.21) * mm, "end": v(99.29, 91.21) * mm});
            skLineSegment(sketch, "E3.16.15.1", {"start": v(103.91, 86.59) * mm, "end": v(103.91, 91.21) * mm});
            skLineSegment(sketch, "E3.16.15.2", {"start": v(103.91, 86.59) * mm, "end": v(99.29, 86.59) * mm});
            skLineSegment(sketch, "E3.16.15.3", {"start": v(99.29, 86.59) * mm, "end": v(99.29, 91.21) * mm});
            skLineSegment(sketch, "E3.16.16.0", {"start": v(103.91, 103.91) * mm, "end": v(99.29, 103.91) * mm});
            skLineSegment(sketch, "E3.16.16.1", {"start": v(103.91, 99.29) * mm, "end": v(103.91, 103.91) * mm});
            skLineSegment(sketch, "E3.16.16.2", {"start": v(103.91, 99.29) * mm, "end": v(99.29, 99.29) * mm});
            skLineSegment(sketch, "E3.16.16.3", {"start": v(99.29, 99.29) * mm, "end": v(99.29, 103.91) * mm});
            skLineSegment(sketch, "E3.direction1", {"start": v(-103.91, -99.29) * mm, "end": v(-91.21, -99.29) * mm, "construction": true});
            skLineSegment(sketch, "E3.direction2", {"start": v(-103.91, -99.29) * mm, "end": v(-103.91, -86.59) * mm, "construction": true});
            skSolve(sketch);
        }
        {
            var Q0;
            Q0 = qSketchRegion(id + "F0", true);
            extrude(context, id + "F1", {"entities" : qUnion([Q0]), "depth" : 3.17 * mm});
        }
    });
